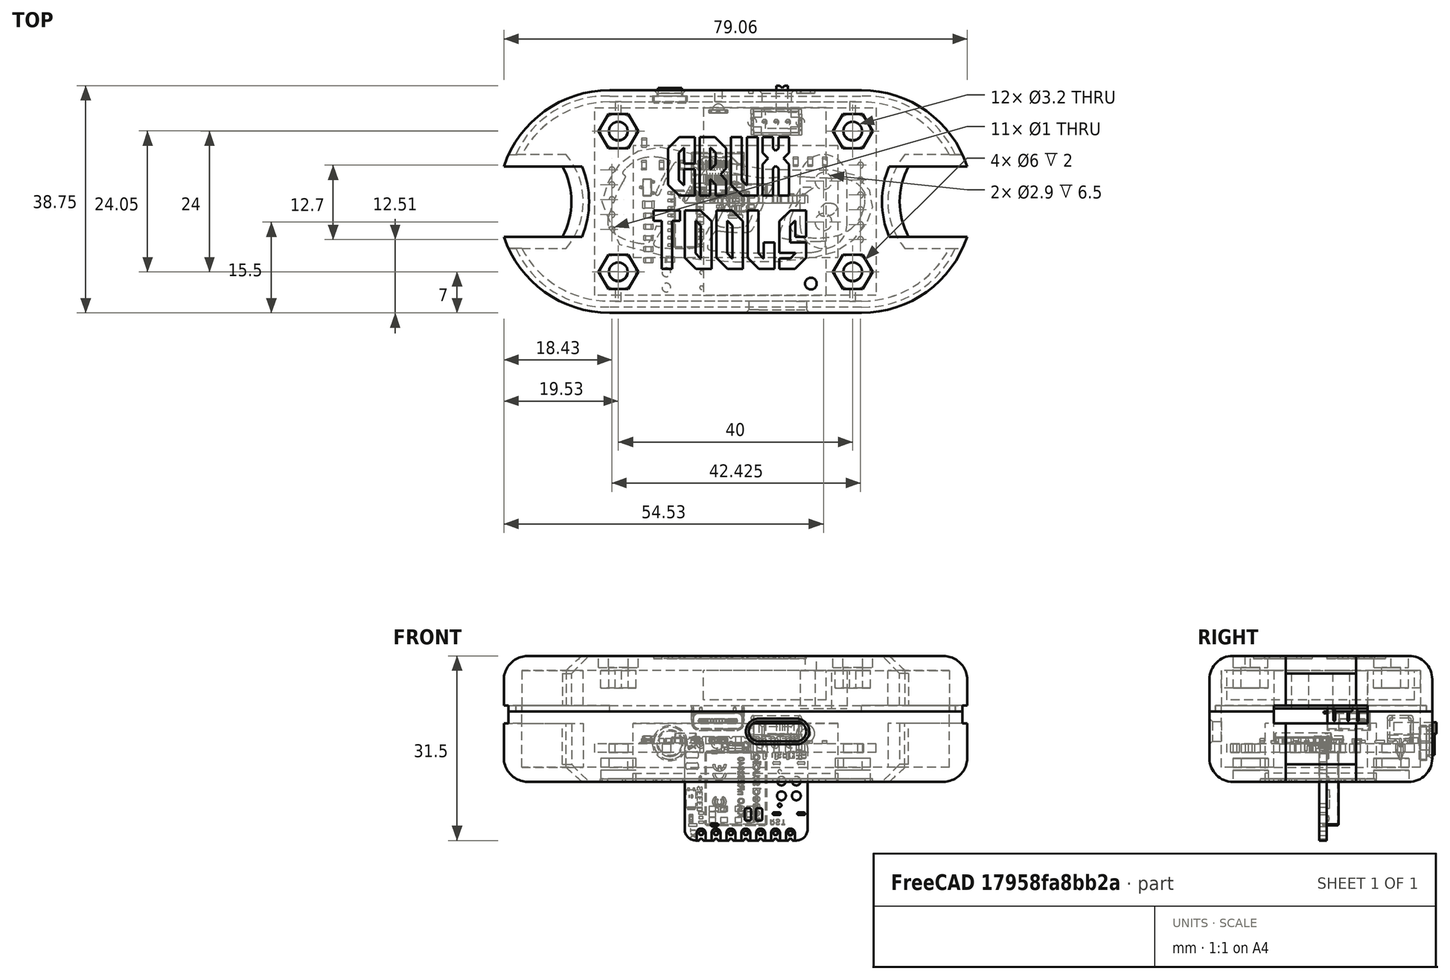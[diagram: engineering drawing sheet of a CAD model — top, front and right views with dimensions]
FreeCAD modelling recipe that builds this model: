
FCSTD DOCUMENT  (FreeCAD 1.0R39285 (Git))
Label: enclosure2
License: All rights reserved
LicenseURL: https://en.wikipedia.org/wiki/All_rights_reserved
objects: Part::Feature×116, Sketcher::SketchObject×53, PartDesign::Pad×51, PartDesign::Body×51, Part::Cut×33, App::Part×17, Part::MultiFuse×8, Part::Extrusion×6, Part::Part2DObjectPython×4, Part::Chamfer×3, Part::FeaturePython×2, Part::Fillet×2, Mesh::Feature×1
note: 484 computed .brp shape members not serialized (recipe doc carries the construction recipe); baked Part::Feature solids carry a one-line shape summary decoded from their .brp

FEATURE [Mesh::Feature] load_cell
  Placement = pos=(0,0,-6.9) rot=(0,0,1;3.14159rad)
FEATURE [Part::Feature] Part__Feature  label="R_0603"
  Placement = pos=(-15.6,10.075,1.595) rot=(0,0,-1;1.5708rad)
  shape: bbox 0.8 x 1.6 x 0.45 mm, 26 faces (baked)
FEATURE [Part::Feature] Part__Feature001  label="R_0604"
  Placement = pos=(-14.8489,-4.2736,1.595) rot=(0,0,1;0rad)
  shape: bbox 1.6 x 0.8 x 0.45 mm, 26 faces (baked)
FEATURE [Part::Feature] Part__Feature002  label="R_0605"
  Placement = pos=(15.22,6.81,1.595) rot=(0,0,-1;1.5708rad)
  shape: bbox 0.8 x 1.6 x 0.45 mm, 26 faces (baked)
FEATURE [Part::Feature] Part__Feature003  label="C_0603"
  Placement = pos=(-3.975,0.675,1.595) rot=(0,0,-1;1.5708rad)
  shape: bbox 0.8 x 1.6 x 0.8 mm, 28 faces (baked)
FEATURE [Part::Feature] Part__Feature004  label="LED-ARRAY-SMD_4P-L3.2-W1.5-H1.0"
  Placement = pos=(-2.94,15.1358,2.095) rot=(0,0,1;0rad)
  shape: bbox 2 x 1 x 1 mm, 5 faces (baked)
FEATURE [Part::Feature] Part__Feature005  label="LED-ARRAY-SMD_4P-L3.2-W1.5-H1.001"
  Placement = pos=(-2.94,15.1358,2.095) rot=(0,0,1;0rad)
  shape: bbox 3.22 x 0.52 x 1.02 mm, 354 faces (baked)
FEATURE [App::Part] LED_ARRAY_SMD_4P_L3_2_W1_5_H1_0  label="LED-ARRAY-SMD_4P-L3.2-W1.5-H1.002"
  Group = -> [Part__Feature004,Part__Feature005]
  Origin = -> Origin020
FEATURE [Part::Feature] Part__Feature006  label="C_0604"
  Placement = pos=(-6.025,6.18,1.595) rot=(0,0,1;1.5708rad)
  shape: bbox 0.8 x 1.6 x 0.8 mm, 28 faces (baked)
FEATURE [Part::Feature] Part__Feature007  label="C_0605"
  Placement = pos=(-11.2489,-9.9886,1.595) rot=(0,0,1;3.14159rad)
  shape: bbox 1.6 x 0.8 x 0.8 mm, 28 faces (baked)
FEATURE [Part::Feature] Part__Feature008  label="R_0606"
  Placement = pos=(12.72,6.81,1.595) rot=(0,0,-1;1.5708rad)
  shape: bbox 0.8 x 1.6 x 0.45 mm, 26 faces (baked)
FEATURE [Part::Feature] Part__Feature009  label="SOIC-16_3.9x9.9mm_P1.27mm"
  Placement = pos=(-8.4989,-3.0036,1.595) rot=(0,0,1;0rad)
  shape: bbox 6 x 9.9 x 1.75 mm, 276 faces (baked)
FEATURE [Part::Feature] Part__Feature010  label="R_0607"
  Placement = pos=(10.22,6.81,1.595) rot=(0,0,-1;1.5708rad)
  shape: bbox 0.8 x 1.6 x 0.45 mm, 26 faces (baked)
FEATURE [Part::Feature] Part__Feature011  label="L_0805"
  Placement = pos=(-14.85,-0.5,1.595) rot=(0,0,1;0rad)
  shape: bbox 2 x 1.25 x 1.25 mm, 28 faces (baked)
FEATURE [Part::Feature] Part__Feature012  label="C_0606"
  Placement = pos=(-14.8489,-6.1786,1.595) rot=(0,0,1;0rad)
  shape: bbox 1.6 x 0.8 x 0.8 mm, 28 faces (baked)
FEATURE [Part::Feature] Part__Feature013  label="Pocket008"
  shape: bbox 2.35 x 3.4 x 1.6 mm, 27 faces (baked)
FEATURE [Part::Feature] Part__Feature014  label="Body001"
  shape: bbox 2.35 x 3.4 x 1.6 mm, 27 faces (baked)
FEATURE [Part::Feature] Part__Feature015  label="Fusion"
  shape: bbox 4.7 x 3.5 x 1.15 mm, 156 faces (baked)
FEATURE [Part::Feature] Part__Feature016  label="Pad007"
  shape: bbox 1.35 x 0.6 x 0.1 mm, 7 faces (baked)
FEATURE [Part::Feature] Part__Feature017  label="Pocket008_(Mirror_#2)"
  shape: bbox 2.35 x 3.4 x 1.6 mm, 27 faces (baked)
FEATURE [Part::Feature] Part__Feature018  label="Body002"
  shape: bbox 2.4 x 4.1 x 1.4 mm, 32 faces (baked)
FEATURE [Part::Feature] Part__Feature019  label="Pocket011"
  shape: bbox 2.4 x 4.1 x 1.4 mm, 17 faces (baked)
FEATURE [Part::Feature] Part__Feature020  label="Pad007_(Mirror_#3)"
  shape: bbox 1.35 x 0.6 x 0.1 mm, 7 faces (baked)
FEATURE [Part::Feature] Part__Feature021  label="Pad007_(Mirror_#5)"
  shape: bbox 1.35 x 0.6 x 0.1 mm, 7 faces (baked)
FEATURE [Part::Feature] Part__Feature022  label="Pad007_(Mirror_#4)"
  shape: bbox 1.35 x 0.6 x 0.1 mm, 7 faces (baked)
FEATURE [App::Part] Panasonic_EVQPUJ_EVQPUA
  Group = -> [Part__Feature013,Part__Feature014,Part__Feature015,Part__Feature016,Part__Feature017,Part__Feature018,Part__Feature019,Part__Feature020,Part__Feature021,Part__Feature022]
  Origin = -> Origin021
  Placement = pos=(-11.125,14.025,1.595) rot=(0,0,1;3.14159rad)
FEATURE [Part::Feature] Part__Feature023  label="R_0608"
  Placement = pos=(-14.8489,-8.0836,1.595) rot=(0,0,1;0rad)
  shape: bbox 1.6 x 0.8 x 0.45 mm, 26 faces (baked)
FEATURE [Part::Feature] Part__Feature024  label="R_0609"
  Placement = pos=(-14.8489,-9.9886,1.595) rot=(0,0,1;0rad)
  shape: bbox 1.6 x 0.8 x 0.45 mm, 26 faces (baked)
FEATURE [Part::Feature] Part__Feature025  label="C_0607"
  Placement = pos=(-15.6,6.18,1.595) rot=(0,0,1;1.5708rad)
  shape: bbox 0.8 x 1.6 x 0.8 mm, 28 faces (baked)
FEATURE [Part::Feature] Part__Feature026  label="C_0608"
  Placement = pos=(-9.025,6.18,1.595) rot=(0,0,1;1.5708rad)
  shape: bbox 0.8 x 1.6 x 0.8 mm, 28 faces (baked)
FEATURE [Part::Feature] Part__Feature027  label="BOSS-EXTRUDE14_8_"
  Placement = pos=(-3.0192,1.09628,5.395) rot=(0,0,1;0rad)
  shape: bbox 0.6 x 1 x 0.3 mm, 6 faces (baked)
FEATURE [Part::Feature] Part__Feature028  label="BOSS-EXTRUDE7_4_"
  Placement = pos=(-3.0192,1.09628,5.395) rot=(0,0,1;0rad)
  shape: bbox 0.3 x 3.784 x 0.75 mm, 6 faces (baked)
FEATURE [Part::Feature] Part__Feature029  label="BOSS-EXTRUDE7_3_"
  Placement = pos=(-3.0192,1.09628,5.395) rot=(0,0,1;0rad)
  shape: bbox 0.3 x 3.784 x 0.75 mm, 6 faces (baked)
FEATURE [Part::Feature] Part__Feature030  label="BOSS-EXTRUDE14_4_"
  Placement = pos=(-3.0192,1.09628,5.395) rot=(0,0,1;0rad)
  shape: bbox 0.3 x 1 x 0.3 mm, 6 faces (baked)
FEATURE [Part::Feature] Part__Feature031  label="BOSS-EXTRUDE14_2_"
  Placement = pos=(-3.0192,1.09628,5.395) rot=(0,0,1;0rad)
  shape: bbox 0.6 x 1 x 0.3 mm, 6 faces (baked)
FEATURE [Part::Feature] Part__Feature032  label="BOSS-EXTRUDE14_11_"
  Placement = pos=(-3.0192,1.09628,5.395) rot=(0,0,1;0rad)
  shape: bbox 0.3 x 1 x 0.3 mm, 6 faces (baked)
FEATURE [Part::Feature] Part__Feature033  label="BOSS-EXTRUDE7_7_"
  Placement = pos=(-3.0192,1.09628,5.395) rot=(0,0,1;0rad)
  shape: bbox 0.3 x 3.784 x 0.75 mm, 6 faces (baked)
FEATURE [Part::Feature] Part__Feature034  label="BOSS-EXTRUDE14_9_"
  Placement = pos=(-3.0192,1.09628,5.395) rot=(0,0,1;0rad)
  shape: bbox 0.3 x 1 x 0.3 mm, 6 faces (baked)
FEATURE [Part::Feature] Part__Feature035  label="BOSS-EXTRUDE14_3_"
  Placement = pos=(-3.0192,1.09628,5.395) rot=(0,0,1;0rad)
  shape: bbox 0.3 x 1 x 0.3 mm, 6 faces (baked)
FEATURE [Part::Feature] Part__Feature036  label="BOSS-EXTRUDE14_7_"
  Placement = pos=(-3.0192,1.09628,5.395) rot=(0,0,1;0rad)
  shape: bbox 0.6 x 1 x 0.3 mm, 6 faces (baked)
FEATURE [Part::Feature] Part__Feature037  label="MIRROR2"
  Placement = pos=(-3.0192,1.09628,5.395) rot=(0,0,1;0rad)
  shape: bbox 6.7 x 4.6 x 0.7 mm, 26 faces (baked)
FEATURE [Part::Feature] Part__Feature038  label="BOSS-EXTRUDE14_5_"
  Placement = pos=(-3.0192,1.09628,5.395) rot=(0,0,1;0rad)
  shape: bbox 0.3 x 1 x 0.3 mm, 6 faces (baked)
FEATURE [Part::Feature] Part__Feature039  label="BOSS-EXTRUDE14_12_"
  Placement = pos=(-3.0192,1.09628,5.395) rot=(0,0,1;0rad)
  shape: bbox 0.3 x 1 x 0.3 mm, 6 faces (baked)
FEATURE [Part::Feature] Part__Feature040  label="BOSS-EXTRUDE7_8_"
  Placement = pos=(-3.0192,1.09628,5.395) rot=(0,0,1;0rad)
  shape: bbox 0.3 x 3.784 x 0.75 mm, 6 faces (baked)
FEATURE [Part::Feature] Part__Feature041  label="BOSS-EXTRUDE7_1_"
  Placement = pos=(-3.0192,1.09628,5.395) rot=(0,0,1;0rad)
  shape: bbox 0.3 x 3.784 x 0.75 mm, 6 faces (baked)
FEATURE [Part::Feature] Part__Feature042  label="BOSS-EXTRUDE14_10_"
  Placement = pos=(-3.0192,1.09628,5.395) rot=(0,0,1;0rad)
  shape: bbox 0.3 x 1 x 0.3 mm, 6 faces (baked)
FEATURE [Part::Feature] Part__Feature043  label="BOSS-EXTRUDE7_9_"
  Placement = pos=(-3.0192,1.09628,5.395) rot=(0,0,1;0rad)
  shape: bbox 0.3 x 3.784 x 0.75 mm, 6 faces (baked)
FEATURE [Part::Feature] Part__Feature044  label="BOSS-EXTRUDE14_6_"
  Placement = pos=(-3.0192,1.09628,5.395) rot=(0,0,1;0rad)
  shape: bbox 0.6 x 1 x 0.3 mm, 6 faces (baked)
FEATURE [Part::Feature] Part__Feature045  label="CHAMFER9"
  Placement = pos=(-3.0192,1.09628,5.395) rot=(0,0,1;0rad)
  shape: bbox 8.94 x 7.3 x 4.2 mm, 103 faces (baked)
FEATURE [Part::Feature] Part__Feature046  label="BOSS-EXTRUDE14_1_"
  Placement = pos=(-3.0192,1.09628,5.395) rot=(0,0,1;0rad)
  shape: bbox 0.3 x 1 x 0.3 mm, 6 faces (baked)
FEATURE [Part::Feature] Part__Feature047  label="BOSS-EXTRUDE7_6_"
  Placement = pos=(-3.0192,1.09628,5.395) rot=(0,0,1;0rad)
  shape: bbox 0.3 x 3.784 x 0.75 mm, 6 faces (baked)
FEATURE [Part::Feature] Part__Feature048  label="BOSS-EXTRUDE7_2_"
  Placement = pos=(-3.0192,1.09628,5.395) rot=(0,0,1;0rad)
  shape: bbox 0.3 x 3.784 x 0.75 mm, 6 faces (baked)
FEATURE [Part::Feature] Part__Feature049  label="CUT-EXTRUDE5"
  Placement = pos=(-3.0192,1.09628,5.395) rot=(0,0,1;0rad)
  shape: bbox 8.867 x 2 x 3.668 mm, 129 faces (baked)
FEATURE [Part::Feature] Part__Feature050  label="BOSS-EXTRUDE7_5_"
  Placement = pos=(-3.0192,1.09628,5.395) rot=(0,0,1;0rad)
  shape: bbox 0.3 x 3.784 x 0.75 mm, 6 faces (baked)
FEATURE [App::Part] USB_TYPE_C_PORT__1_  label="USB TYPE C PORT (1)"
  Group = -> [Part__Feature027,Part__Feature028,Part__Feature029,Part__Feature030,Part__Feature031,Part__Feature032,Part__Feature033,Part__Feature034,Part__Feature035,Part__Feature036,Part__Feature037,Part__Feature038,Part__Feature039,Part__Feature040,Part__Feature041,Part__Feature042,Part__Feature043,Part__Feature044,Part__Feature045,Part__Feature046,Part__Feature047,Part__Feature048,Part__Feature049,+1 more]
  Origin = -> Origin022
  Placement = pos=(-3.0192,1.09628,5.395) rot=(0,0,1;0rad)
FEATURE [App::Part] USB_TYPE_C_PORT  label="USB TYPE C PORT"
  Group = -> [USB_TYPE_C_PORT__1_]
  Origin = -> Origin023
  Placement = pos=(4.31609,13.395,-12.1571) rot=(0.57735,0.57735,-0.57735;2.0944rad)
FEATURE [Part::Feature] Part__Feature051  label="Shield"
  Placement = pos=(-0.225,0,0) rot=(0,0,1;0rad)
  shape: bbox 10.6 x 2.7 x 12.6 mm, 38 faces (baked)
FEATURE [Part::Feature] Part__Feature052  label="Body"
  Placement = pos=(0,0,0.1) rot=(0,0,1;0rad)
  shape: bbox 2.6 x 1.6 x 0.63 mm, 10 faces (baked)
FEATURE [Part::Feature] Part__Feature053  label="Pins"
  shape: bbox 0.44 x 0.44 x 0.1 mm, 6 faces (baked)
FEATURE [Part::Feature] Part__Feature054  label="Pins001"
  shape: bbox 0.44 x 0.44 x 0.1 mm, 6 faces (baked)
FEATURE [Part::Feature] Part__Feature055  label="Pins002"
  shape: bbox 0.44 x 0.44 x 0.1 mm, 6 faces (baked)
FEATURE [Part::Feature] Part__Feature056  label="Pins003"
  shape: bbox 0.44 x 0.44 x 0.1 mm, 6 faces (baked)
FEATURE [App::Part] Pins  label="Pins004"
  Group = -> [Part__Feature053,Part__Feature054,Part__Feature055,Part__Feature056]
  Origin = -> Origin024
FEATURE [App::Part] SKTAAAE010_v1  label="SKTAAAE010 v1"
  Group = -> [Part__Feature052,Pins]
  Origin = -> Origin025
  Placement = pos=(10.4051,1,-11.8268) rot=(-1,0,0;1.5708rad)
FEATURE [Part::Feature] Part__Feature057  label="CAP"
  shape: bbox 0.3048 x 0.3 x 0.3096 mm, 6 faces (baked)
FEATURE [Part::Feature] Part__Feature058  label="CAP001"
  shape: bbox 0.3048 x 0.3 x 0.15 mm, 16 faces (baked)
FEATURE [Part::Feature] Part__Feature059  label="CAP002"
  shape: bbox 0.3048 x 0.3 x 0.15 mm, 16 faces (baked)
FEATURE [App::Part] CAP  label="CAP003"
  Group = -> [Part__Feature057,Part__Feature058,Part__Feature059]
  Origin = -> Origin026
FEATURE [Part::Feature] Part__Feature060  label="ANT1"
  shape: bbox 1.6 x 0.5 x 3.2 mm, 21 faces (baked)
FEATURE [Part::Feature] Part__Feature061  label="ANT002"
  shape: bbox 0.2997 x 0.01 x 0.5004 mm, 10 faces (baked)
FEATURE [Part::Feature] Part__Feature062  label="ANT003"
  shape: bbox 0.05 x 0.01 x 0.5004 mm, 6 faces (baked)
FEATURE [App::Part] ANT1  label="ANT004"
  Group = -> [Part__Feature060,Part__Feature061,Part__Feature062]
  Origin = -> Origin027
FEATURE [Part::Feature] Part__Feature063  label="Silkscreen"
  shape: bbox 0.8405 x 0.01 x 0.5826 mm, 14 faces (baked)
FEATURE [Part::Feature] Part__Feature064  label="Silkscreen001"
  shape: bbox 0.8378 x 0.01 x 0.5436 mm, 10 faces (baked)
FEATURE [Part::Feature] Part__Feature065  label="Silkscreen002"
  shape: bbox 0.6266 x 0.01 x 0.9136 mm, 26 faces (baked)
FEATURE [Part::Feature] Part__Feature066  label="Silkscreen003"
  shape: bbox 0.8636 x 0.01 x 0.6016 mm, 14 faces (baked)
FEATURE [Part::Feature] Part__Feature067  label="Silkscreen004"
  shape: bbox 0.6266 x 0.01 x 0.9136 mm, 26 faces (baked)
FEATURE [Part::Feature] Part__Feature068  label="Silkscreen005"
  shape: bbox 0.5766 x 0.01 x 0.8886 mm, 10 faces (baked)
FEATURE [Part::Feature] Part__Feature069  label="Silkscreen006"
  shape: bbox 0.9136 x 0.01 x 0.6193 mm, 18 faces (baked)
FEATURE [Part::Feature] Part__Feature070  label="Silkscreen007"
  shape: bbox 0.8555 x 0.01 x 0.5936 mm, 20 faces (baked)
FEATURE [Part::Feature] Part__Feature071  label="Silkscreen008"
  shape: bbox 0.6266 x 0.01 x 0.9063 mm, 20 faces (baked)
FEATURE [Part::Feature] Part__Feature072  label="Silkscreen009"
  shape: bbox 0.624 x 0.01 x 0.8886 mm, 14 faces (baked)
FEATURE [Part::Feature] Part__Feature073  label="Silkscreen010"
  shape: bbox 0.624 x 0.01 x 0.9063 mm, 20 faces (baked)
FEATURE [Part::Feature] Part__Feature074  label="Silkscreen011"
  shape: bbox 0.8406 x 0.01 x 0.5851 mm, 14 faces (baked)
FEATURE [Part::Feature] Part__Feature075  label="Silkscreen012"
  shape: bbox 0.635 x 0.01 x 1.397 mm, 10 faces (baked)
FEATURE [App::Part] Silkscreen  label="Silkscreen013"
  Group = -> [Part__Feature063,Part__Feature064,Part__Feature065,Part__Feature066,Part__Feature067,Part__Feature068,Part__Feature069,Part__Feature070,Part__Feature071,Part__Feature072,Part__Feature073,Part__Feature074,Part__Feature075]
  Origin = -> Origin028
FEATURE [Part::Feature] Part__Feature076  label="CAP004"
  Placement = pos=(-1.90636,0,5.2077) rot=(0,0,1;0rad)
  shape: bbox 0.3048 x 0.3 x 0.3096 mm, 6 faces (baked)
FEATURE [Part::Feature] Part__Feature077  label="CAP005"
  Placement = pos=(-1.90636,0,5.2077) rot=(0,0,1;0rad)
  shape: bbox 0.3048 x 0.3 x 0.15 mm, 16 faces (baked)
FEATURE [Part::Feature] Part__Feature078  label="CAP006"
  Placement = pos=(-1.90636,0,5.2077) rot=(0,0,1;0rad)
  shape: bbox 0.3048 x 0.3 x 0.15 mm, 16 faces (baked)
FEATURE [App::Part] CAP001  label="CAP007"
  Group = -> [Part__Feature076,Part__Feature077,Part__Feature078]
  Origin = -> Origin029
FEATURE [Part::Feature] Part__Feature079  label="CAP 3"
  shape: bbox 0.435 x 0.4 x 0.397 mm, 10 faces (baked)
FEATURE [Part::Feature] Part__Feature080  label="CAP 004"
  shape: bbox 0.435 x 0.4 x 0.3 mm, 18 faces (baked)
FEATURE [Part::Feature] Part__Feature081  label="CAP 005"
  shape: bbox 0.435 x 0.4 x 0.3 mm, 18 faces (baked)
FEATURE [App::Part] CAP_3  label="CAP 006"
  Group = -> [Part__Feature079,Part__Feature080,Part__Feature081]
  Origin = -> Origin030
FEATURE [Part::Feature] Part__Feature082  label="LED"
  shape: bbox 0.635 x 0.3 x 0.87 mm, 9 faces (baked)
FEATURE [Part::Feature] Part__Feature083  label="LED001"
  shape: bbox 0.381 x 0.3 x 0.1905 mm, 5 faces (baked)
FEATURE [Part::Feature] Part__Feature084  label="LED002"
  shape: bbox 0.635 x 0.3 x 0.2 mm, 18 faces (baked)
FEATURE [Part::Feature] Part__Feature085  label="LED003"
  shape: bbox 0.635 x 0.3 x 0.2 mm, 8 faces (baked)
FEATURE [App::Part] LED  label="LED004"
  Group = -> [Part__Feature082,Part__Feature083,Part__Feature084,Part__Feature085]
  Origin = -> Origin031
FEATURE [Part::Feature] Part__Feature086  label="USR"
  shape: bbox 1.001 x 0.3 x 1.001 mm, 7 faces (baked)
FEATURE [Part::Feature] Part__Feature087  label="COMPOUND"
  shape: bbox 20.96 x 1.25 x 17.78 mm, 684 faces (baked)
FEATURE [Part::Feature] Part__Feature088  label="COMPOUND001"
  shape: bbox 0.3302 x 0.01 x 0.3302 mm, 6 faces (baked)
FEATURE [Part::Feature] Part__Feature089  label="COMPOUND002"
  shape: bbox 0.3302 x 0.01 x 0.3302 mm, 6 faces (baked)
FEATURE [Part::Feature] Part__Feature090  label="COMPOUND003"
  shape: bbox 0.3302 x 0.01 x 0.3302 mm, 6 faces (baked)
FEATURE [Part::Feature] Part__Feature091  label="COMPOUND004"
  shape: bbox 0.3302 x 0.01 x 0.3302 mm, 6 faces (baked)
FEATURE [Part::Feature] Part__Feature092  label="COMPOUND005"
  shape: bbox 0.2489 x 0.01 x 0.07366 mm, 6 faces (baked)
FEATURE [Part::Feature] Part__Feature093  label="COMPOUND006"
  shape: bbox 0.3658 x 0.01 x 0.3607 mm, 6 faces (baked)
FEATURE [Part::Feature] Part__Feature094  label="COMPOUND007"
  shape: bbox 0.4318 x 0.01 x 0.3658 mm, 6 faces (baked)
FEATURE [Part::Feature] Part__Feature095  label="COMPOUND008"
  shape: bbox 0.4318 x 0.01 x 0.3658 mm, 6 faces (baked)
FEATURE [Part::Feature] Part__Feature096  label="COMPOUND009"
  shape: bbox 1.29 x 0.01 x 0.3861 mm, 6 faces (baked)
FEATURE [Part::Feature] Part__Feature097  label="COMPOUND010"
  shape: bbox 0.3658 x 0.01 x 0.3607 mm, 6 faces (baked)
FEATURE [Part::Feature] Part__Feature098  label="COMPOUND011"
  shape: bbox 0.2489 x 0.01 x 0.1397 mm, 6 faces (baked)
FEATURE [Part::Feature] Part__Feature099  label="COMPOUND012"
  shape: bbox 2.111 x 0.01 x 1.09 mm, 10 faces (baked)
FEATURE [Part::Feature] Part__Feature100  label="COMPOUND013"
  shape: bbox 2.111 x 0.01 x 1.095 mm, 10 faces (baked)
FEATURE [Part::Feature] Part__Feature101  label="COMPOUND014"
  shape: bbox 1.095 x 0.01 x 2.111 mm, 10 faces (baked)
FEATURE [Part::Feature] Part__Feature102  label="COMPOUND015"
  shape: bbox 1.095 x 0.01 x 2.111 mm, 10 faces (baked)
FEATURE [App::Part] COMPOUND  label="COMPOUND016"
  Group = -> [Part__Feature087,Part__Feature088,Part__Feature089,Part__Feature090,Part__Feature091,Part__Feature092,Part__Feature093,Part__Feature094,Part__Feature095,Part__Feature096,Part__Feature097,Part__Feature098,Part__Feature099,Part__Feature100,Part__Feature101,Part__Feature102]
  Origin = -> Origin032
FEATURE [App::Part] PCB__1_  label="PCB (1)"
  Group = -> [CAP,ANT1,Silkscreen,CAP001,CAP_3,LED,Part__Feature086,COMPOUND]
  Origin = -> Origin033
FEATURE [Part::Feature] Part__Feature103  label="SOLID"
  shape: bbox 10.2 x 0.02 x 12.2 mm, 800 faces (baked)
FEATURE [App::Part] XIAO_nRF52840_v3  label="XIAO-nRF52840 v3"
  Group = -> [USB_TYPE_C_PORT,Part__Feature051,SKTAAAE010_v1,PCB__1_,Part__Feature103]
  Origin = -> Origin034
  Placement = pos=(1.04,-3.4715,1.595) rot=(0.57735,-0.57735,-0.57735;2.0944rad)
FEATURE [Part::Feature] Part__Feature104  label="C_0609"
  Placement = pos=(-12.6,6.18,1.595) rot=(0,0,1;1.5708rad)
  shape: bbox 0.8 x 1.6 x 0.8 mm, 28 faces (baked)
FEATURE [Part::Feature] Part__Feature105  label="SOT-23-3"
  Placement = pos=(-15.1,2.4,1.595) rot=(0,0,1;3.14159rad)
  shape: bbox 2.5 x 3 x 1.2 mm, 69 faces (baked)
FEATURE [Part::Feature] Part__Feature106  label="SW_Slide_SPDT_Angled_CK_OS102011MA1Q"
  Placement = pos=(8.95,13.55,1.595) rot=(0,0,1;3.14159rad)
  shape: bbox 8.6 x 4.4 x 7.5 mm, 156 faces (baked)
FEATURE [Part::Feature] Part__Feature107  label="SW_Slide_SPDT_Angled_CK_OS102011MA1Q001"
  Placement = pos=(8.95,13.55,1.595) rot=(0,0,1;3.14159rad)
  shape: bbox 7.7 x 4.4 x 0.6 mm, 14 faces (baked)
FEATURE [Part::Feature] Part__Feature108  label="SW_Slide_SPDT_Angled_CK_OS102011MA1Q002"
  Placement = pos=(8.95,13.55,1.595) rot=(0,0,1;3.14159rad)
  shape: bbox 5.6 x 7.3 x 2 mm, 21 faces (baked)
FEATURE [Part::Feature] Part__Feature109  label="SW_Slide_SPDT_Angled_CK_OS102011MA1Q003"
  Placement = pos=(8.95,13.55,1.595) rot=(0,0,1;3.14159rad)
  shape: bbox 0.5 x 0.3 x 3.6 mm, 8 faces (baked)
FEATURE [Part::Feature] Part__Feature110  label="SW_Slide_SPDT_Angled_CK_OS102011MA1Q004"
  Placement = pos=(8.95,13.55,1.595) rot=(0,0,1;3.14159rad)
  shape: bbox 0.5 x 0.3 x 3.6 mm, 8 faces (baked)
FEATURE [Part::Feature] Part__Feature111  label="SW_Slide_SPDT_Angled_CK_OS102011MA1Q005"
  Placement = pos=(8.95,13.55,1.595) rot=(0,0,1;3.14159rad)
  shape: bbox 0.5 x 0.3 x 3.6 mm, 8 faces (baked)
FEATURE [App::Part] SW_Slide_SPDT_Angled_CK_OS102011MA1Q  label="SW_Slide_SPDT_Angled_CK_OS102011MA1Q006"
  Group = -> [Part__Feature106,Part__Feature107,Part__Feature108,Part__Feature109,Part__Feature110,Part__Feature111]
  Origin = -> Origin035
FEATURE [Part::Feature] Part__Feature112  label="R_0603_1608Metric"
  Placement = pos=(-14.8489,-2.3686,1.595) rot=(0,0,1;0rad)
  shape: bbox 1.6 x 0.8 x 0.45 mm, 26 faces (baked)
FEATURE [Part::Feature] Part__Feature113  label="mito_PCB"
  shape: bbox 48 x 32 x 1.51 mm, 30 faces (baked)
FEATURE [App::Part] mito_1  label="mito 1"
  Group = -> [Part__Feature,Part__Feature001,Part__Feature002,Part__Feature003,LED_ARRAY_SMD_4P_L3_2_W1_5_H1_0,Part__Feature006,Part__Feature007,Part__Feature008,Part__Feature009,Part__Feature010,Part__Feature011,Part__Feature012,Panasonic_EVQPUJ_EVQPUA,Part__Feature023,Part__Feature024,Part__Feature025,Part__Feature026,XIAO_nRF52840_v3,Part__Feature104,Part__Feature105,SW_Slide_SPDT_Angled_CK_OS102011MA1Q,+2 more]
  Origin = -> Origin036
  Placement = pos=(0,-8e-16,-1) rot=(1,0,0;0rad)
FEATURE [Sketcher::SketchObject] Sketch003
  ArcFitTolerance = 1e-06
  AttachmentSupport = -> [XY_Plane037]
  FullyConstrained = true
  MakeInternals = false
  MapMode = 5
  sketch-geometry (4):
    g0: LineSegment StartX=-16 StartY=10.5 StartZ=0 EndX=-16 EndY=-10.5 EndZ=0
    g1: LineSegment StartX=-16 StartY=-10.5 StartZ=0 EndX=16 EndY=-10.5 EndZ=0
    g2: LineSegment StartX=16 StartY=-10.5 StartZ=0 EndX=16 EndY=10.5 EndZ=0
    g3: LineSegment StartX=16 StartY=10.5 StartZ=0 EndX=-16 EndY=10.5 EndZ=0
  constraints (11):
    c: Coincident(g0,g1)
    c: Coincident(g1,g2)
    c: Coincident(g2,g3)
    c: Coincident(g3,g0)
    c: Vertical(g0)
    c: Vertical(g2)
    c: Horizontal(g1)
    c: Horizontal(g3)
    c: Symmetric(g0,g1,g-1)
    c: DistanceX(g3,g3) = 32
    c: DistanceY(g2,g2) = 21
FEATURE [PartDesign::Pad] Pad003
  Direction = (0,0,1)
  Length = 5
  Length2 = 10
  Profile = -> Sketch003
  ReferenceAxis = -> Sketch003 [N_Axis]
  Refine = true
  Suppressed = false
  Type = 0
FEATURE [PartDesign::Body] Body003  label="Battery"
  AllowCompound = false
  Group = -> [Sketch003,Pad003]
  Origin = -> Origin037
  Placement = pos=(5,-2.3e-15,9) rot=(0,0,1;4.71239rad)
  Tip = -> Pad003
FEATURE [Sketcher::SketchObject] Sketch
  ArcFitTolerance = 1e-06
  AttachmentOffset = pos=(0,0,-5) rot=(0,0,1;0rad)
  AttachmentSupport = -> [XY_Plane]
  FullyConstrained = true
  MakeInternals = false
  MapMode = 5
  Placement = pos=(0,0,-5) rot=(0,0,1;0rad)
  sketch-geometry (18):
    g0: ArcOfCircle [constr] CenterX=-21.5 CenterY=1.5e-15 CenterZ=0 NormalX=0 NormalY=0 NormalZ=1 AngleXU=0 Radius=19 StartAngle=1.5708 EndAngle=4.71239
    g1: ArcOfCircle [constr] CenterX=21.5 CenterY=2.06e-14 CenterZ=0 NormalX=0 NormalY=0 NormalZ=1 AngleXU=0 Radius=19 StartAngle=4.71239 EndAngle=7.85398
    g2: LineSegment [constr] StartX=-21.5 StartY=19 StartZ=0 EndX=21.5 EndY=19 EndZ=0
    g3: LineSegment [constr] StartX=-21.5 StartY=-19 StartZ=0 EndX=21.5 EndY=-19 EndZ=0
    g4: LineSegment StartX=-21.5 StartY=19 StartZ=0 EndX=21.5 EndY=19 EndZ=0
    g5: LineSegment StartX=21.5 StartY=-19 StartZ=0 EndX=-21.5 EndY=-19 EndZ=0
    g6: Circle [constr] CenterX=-40.5 CenterY=0 CenterZ=0 NormalX=0 NormalY=0 NormalZ=1 AngleXU=0 Radius=12.5
    g7: Circle [constr] CenterX=40.5 CenterY=0 CenterZ=0 NormalX=0 NormalY=0 NormalZ=1 AngleXU=0 Radius=12.5
    g8: LineSegment StartX=39.5278 StartY=6 StartZ=0 EndX=29.5341 EndY=6 EndZ=0
    g9: LineSegment StartX=39.5278 StartY=-6 StartZ=0 EndX=29.5341 EndY=-6 EndZ=0
    g10: ArcOfCircle CenterX=40.4557 CenterY=1.6e-15 CenterZ=0 NormalX=0 NormalY=0 NormalZ=1 AngleXU=0 Radius=12.4612 StartAngle=2.63923 EndAngle=3.64395
    g11: ArcOfCircle CenterX=21.5 CenterY=2.47e-14 CenterZ=0 NormalX=0 NormalY=0 NormalZ=1 AngleXU=0 Radius=19 StartAngle=0.321289 EndAngle=1.5708
    g12: ArcOfCircle CenterX=21.5 CenterY=1.88e-14 CenterZ=0 NormalX=0 NormalY=0 NormalZ=1 AngleXU=0 Radius=19 StartAngle=4.71239 EndAngle=5.9619
    g13: LineSegment StartX=-39.5278 StartY=6 StartZ=0 EndX=-29.5341 EndY=6 EndZ=0
    g14: LineSegment StartX=-39.5278 StartY=-6 StartZ=0 EndX=-29.5341 EndY=-6 EndZ=0
    g15: ArcOfCircle CenterX=-40.4557 CenterY=1.3e-15 CenterZ=0 NormalX=0 NormalY=0 NormalZ=1 AngleXU=0 Radius=12.4612 StartAngle=5.78082 EndAngle=6.78555
    g16: ArcOfCircle CenterX=-21.5 CenterY=4.1e-15 CenterZ=0 NormalX=0 NormalY=0 NormalZ=1 AngleXU=0 Radius=19 StartAngle=1.5708 EndAngle=2.8203
    g17: ArcOfCircle CenterX=-21.5 CenterY=-1.9e-15 CenterZ=0 NormalX=0 NormalY=0 NormalZ=1 AngleXU=0 Radius=19 StartAngle=3.46288 EndAngle=4.71239
  constraints (48):
    c: Tangent(g0,g2) = 1.5708
    c: Tangent(g0,g3) = -1.5708
    c: Tangent(g1,g2) = 1.5708
    c: Tangent(g1,g3) = -1.5708
    c: DistanceX(g2,g2) = 43
    c: Symmetric(g0,g1,g-2)
    c: Symmetric(g0,g0,g-1)
    c: DistanceY(g0,g0) = 38
    c: Coincident(g4,g0)
    c: Coincident(g4,g1)
    c: Coincident(g5,g1)
    c: Coincident(g5,g0)
    c: PointOnObject(g6,g0)
    c: PointOnObject(g6,g-1)
    c: PointOnObject(g7,g-1)
    c: PointOnObject(g7,g1)
    c: Equal(g7,g6)
    c: Diameter(g7) = 25
    c: PointOnObject(g8,g1)
    c: PointOnObject(g8,g7)
    c: Horizontal(g8)
    c: PointOnObject(g9,g1)
    c: PointOnObject(g9,g7)
    c: Horizontal(g9)
    c: DistanceY(g9,g8) = 12
    c: DistanceY(g-1,g8) = 6
    c: Coincident(g10,g8)
    c: Coincident(g10,g9)
    c: Distance(g10) = 12.52
    c: Tangent(g11,g1) = -1.5708
    c: Coincident(g11,g8)
    c: Tangent(g12,g1) = -1.5708
    c: Coincident(g12,g9)
    c: PointOnObject(g13,g0)
    c: PointOnObject(g13,g6)
    c: Horizontal(g13)
    c: PointOnObject(g14,g0)
    c: PointOnObject(g14,g6)
    c: Horizontal(g14)
    c: DistanceY(g14,g13) = 12
    c: DistanceY(g-1,g13) = 6
    c: Coincident(g15,g13)
    c: Coincident(g15,g14)
    c: Distance(g15) = 12.52
    c: Coincident(g16,g13)
    c: Tangent(g16,g0) = -1.5708
    c: Coincident(g17,g14)
    c: Tangent(g17,g0) = -1.5708
FEATURE [PartDesign::Pad] Pad
  Direction = (0,0,1)
  Length = 12
  Length2 = 10
  Profile = -> Sketch
  ReferenceAxis = -> Sketch [N_Axis]
  Refine = true
  Suppressed = false
  Type = 0
FEATURE [PartDesign::Body] Body  label="bottom_outer"
  AllowCompound = false
  Group = -> [Sketch,Pad]
  Origin = -> Origin
  Tip = -> Pad
FEATURE [Sketcher::SketchObject] Sketch004
  ArcFitTolerance = 1e-06
  AttachmentOffset = pos=(0,0,-2.5) rot=(0,0,1;0rad)
  AttachmentSupport = -> [XY_Plane038]
  FullyConstrained = true
  MakeInternals = false
  MapMode = 5
  Placement = pos=(0,0,-2.5) rot=(0,0,1;0rad)
  sketch-geometry (18):
    g0: ArcOfCircle [constr] CenterX=-21.5 CenterY=8e-16 CenterZ=0 NormalX=0 NormalY=0 NormalZ=1 AngleXU=0 Radius=17 StartAngle=1.5708 EndAngle=4.71239
    g1: ArcOfCircle [constr] CenterX=21.5 CenterY=3.56e-14 CenterZ=0 NormalX=0 NormalY=0 NormalZ=1 AngleXU=0 Radius=17 StartAngle=4.71239 EndAngle=7.85398
    g2: LineSegment [constr] StartX=-21.5 StartY=17 StartZ=0 EndX=21.5 EndY=17 EndZ=0
    g3: LineSegment [constr] StartX=-21.5 StartY=-17 StartZ=0 EndX=21.5 EndY=-17 EndZ=0
    g4: LineSegment StartX=-21.5 StartY=17 StartZ=0 EndX=21.5 EndY=17 EndZ=0
    g5: LineSegment StartX=21.5 StartY=-17 StartZ=0 EndX=-21.5 EndY=-17 EndZ=0
    g6: Circle [constr] CenterX=-38.5 CenterY=0 CenterZ=0 NormalX=0 NormalY=0 NormalZ=1 AngleXU=0 Radius=12.5
    g7: Circle [constr] CenterX=38.5 CenterY=0 CenterZ=0 NormalX=0 NormalY=0 NormalZ=1 AngleXU=0 Radius=12.5
    g8: LineSegment StartX=36.5 StartY=8 StartZ=0 EndX=28.8953 EndY=8 EndZ=0
    g9: LineSegment StartX=36.5 StartY=-8 StartZ=0 EndX=28.8953 EndY=-8 EndZ=0
    g10: ArcOfCircle CenterX=38.4647 CenterY=1.1e-15 CenterZ=0 NormalX=0 NormalY=0 NormalZ=1 AngleXU=0 Radius=12.4729 StartAngle=2.44528 EndAngle=3.8379
    g11: ArcOfCircle CenterX=21.5 CenterY=7.2e-15 CenterZ=0 NormalX=0 NormalY=0 NormalZ=1 AngleXU=0 Radius=17 StartAngle=0.489957 EndAngle=1.5708
    g12: ArcOfCircle CenterX=21.5 CenterY=2.43e-14 CenterZ=0 NormalX=0 NormalY=0 NormalZ=1 AngleXU=0 Radius=17 StartAngle=4.71239 EndAngle=5.79323
    g13: LineSegment StartX=-36.5 StartY=8 StartZ=0 EndX=-28.8953 EndY=8 EndZ=0
    g14: LineSegment StartX=-36.5 StartY=-8 StartZ=0 EndX=-28.8953 EndY=-8 EndZ=0
    g15: ArcOfCircle CenterX=-38.4647 CenterY=1.1e-15 CenterZ=0 NormalX=0 NormalY=0 NormalZ=1 AngleXU=0 Radius=12.4729 StartAngle=5.58687 EndAngle=6.9795
    g16: ArcOfCircle CenterX=-21.5 CenterY=-2.3e-14 CenterZ=0 NormalX=0 NormalY=0 NormalZ=1 AngleXU=0 Radius=17 StartAngle=1.5708 EndAngle=2.65164
    g17: ArcOfCircle CenterX=-21.5 CenterY=-1.27e-14 CenterZ=0 NormalX=0 NormalY=0 NormalZ=1 AngleXU=0 Radius=17 StartAngle=3.63155 EndAngle=4.71239
  constraints (48):
    c: Tangent(g0,g2) = 1.5708
    c: Tangent(g0,g3) = -1.5708
    c: Tangent(g1,g2) = 1.5708
    c: Tangent(g1,g3) = -1.5708
    c: DistanceX(g2,g2) = 43
    c: Symmetric(g0,g1,g-2)
    c: Symmetric(g0,g0,g-1)
    c: DistanceY(g0,g0) = 34
    c: Coincident(g4,g0)
    c: Coincident(g4,g1)
    c: Coincident(g5,g1)
    c: Coincident(g5,g0)
    c: PointOnObject(g6,g0)
    c: PointOnObject(g6,g-1)
    c: PointOnObject(g7,g-1)
    c: PointOnObject(g7,g1)
    c: Equal(g7,g6)
    c: Diameter(g7) = 25
    c: PointOnObject(g8,g1)
    c: PointOnObject(g8,g7)
    c: Horizontal(g8)
    c: PointOnObject(g9,g1)
    c: PointOnObject(g9,g7)
    c: Horizontal(g9)
    c: DistanceY(g9,g8) = 16
    c: Coincident(g10,g8)
    c: Coincident(g10,g9)
    c: Tangent(g11,g1) = -1.5708
    c: Coincident(g11,g8)
    c: Tangent(g12,g1) = -1.5708
    c: Coincident(g12,g9)
    c: PointOnObject(g13,g0)
    c: PointOnObject(g13,g6)
    c: Horizontal(g13)
    c: PointOnObject(g14,g0)
    c: PointOnObject(g14,g6)
    c: Horizontal(g14)
    c: DistanceY(g14,g13) = 16
    c: Coincident(g15,g13)
    c: Coincident(g15,g14)
    c: Coincident(g16,g13)
    c: Tangent(g16,g0) = -1.5708
    c: Coincident(g17,g14)
    c: Tangent(g17,g0) = -1.5708
    c: DistanceY(g-1,g13) = 8
    c: Distance(g15) = 17.37
    c: DistanceY(g-1,g8) = 8
    c: Distance(g10) = 17.37
FEATURE [PartDesign::Pad] Pad004
  Direction = (0,0,1)
  Length = 10
  Length2 = 10
  Profile = -> Sketch004
  ReferenceAxis = -> Sketch004 [N_Axis]
  Refine = true
  Suppressed = false
  Type = 0
FEATURE [PartDesign::Body] Body004  label="bottom_inner"
  AllowCompound = false
  Group = -> [Sketch004,Pad004]
  Origin = -> Origin038
  Tip = -> Pad004
FEATURE [Part::Cut] Cut
  Base = -> Body
  Refine = true
  Tool = -> Body004
FEATURE [Sketcher::SketchObject] Sketch005
  ArcFitTolerance = 1e-06
  AttachmentOffset = pos=(0,0,7) rot=(0,0,1;0rad)
  AttachmentSupport = -> [XY_Plane039]
  FullyConstrained = false
  MakeInternals = false
  MapMode = 5
  Placement = pos=(0,0,7) rot=(0,0,1;0rad)
  sketch-geometry (13):
    g0: ArcOfCircle [constr] CenterX=-21.5 CenterY=-8e-16 CenterZ=0 NormalX=0 NormalY=0 NormalZ=1 AngleXU=0 Radius=17 StartAngle=1.5708 EndAngle=4.71239
    g1: ArcOfCircle [constr] CenterX=21.5 CenterY=1.7e-15 CenterZ=0 NormalX=0 NormalY=0 NormalZ=1 AngleXU=0 Radius=17 StartAngle=4.71239 EndAngle=7.85398
    g2: LineSegment [constr] StartX=-21.5 StartY=17 StartZ=0 EndX=21.5 EndY=17 EndZ=0
    g3: LineSegment StartX=-21.5 StartY=17 StartZ=0 EndX=21.5 EndY=17 EndZ=0
    g4: Circle [constr] CenterX=-38.5 CenterY=0 CenterZ=0 NormalX=0 NormalY=0 NormalZ=1 AngleXU=0 Radius=12.5
    g5: Circle [constr] CenterX=38.5 CenterY=0 CenterZ=0 NormalX=0 NormalY=0 NormalZ=1 AngleXU=0 Radius=12.5
    g6: ArcOfCircle CenterX=21.5 CenterY=-2e-16 CenterZ=0 NormalX=0 NormalY=0 NormalZ=1 AngleXU=0 Radius=17 StartAngle=0.488987 EndAngle=1.5708
    g7: ArcOfCircle CenterX=-21.5 CenterY=-1.3e-15 CenterZ=0 NormalX=0 NormalY=0 NormalZ=1 AngleXU=0 Radius=17 StartAngle=1.5708 EndAngle=2.65022
    g8: LineSegment StartX=-21.5 StartY=18 StartZ=0 EndX=21.5 EndY=18 EndZ=0
    g9: LineSegment StartX=-36.4887 StartY=8.02123 StartZ=0 EndX=-37.4887 EndY=8.02123 EndZ=0
    g10: ArcOfCircle CenterX=-22.003 CenterY=1.00744 CenterZ=0 NormalX=0 NormalY=0 NormalZ=1 AngleXU=0 Radius=17 StartAngle=1.54121 EndAngle=2.71631
    g11: LineSegment StartX=36.5078 StartY=7.98544 StartZ=0 EndX=37.5078 EndY=7.98544 EndZ=0
    g12: ArcOfCircle CenterX=22.0059 CenterY=1.00753 CenterZ=0 NormalX=0 NormalY=0 NormalZ=1 AngleXU=0 Radius=17 StartAngle=0.422964 EndAngle=1.60056
  constraints (33):
    c: Tangent(g0,g2) = 1.5708
    c: Tangent(g1,g2) = 1.5708
    c: DistanceX(g2,g2) = 43
    c: Symmetric(g0,g1,g-2)
    c: Symmetric(g0,g0,g-1)
    c: DistanceY(g0,g0) = 34
    c: Coincident(g3,g0)
    c: Coincident(g3,g1)
    c: PointOnObject(g4,g0)
    c: PointOnObject(g4,g-1)
    c: PointOnObject(g5,g-1)
    c: PointOnObject(g5,g1)
    c: Equal(g5,g4)
    c: Diameter(g5) = 25
    c: PointOnObject(g6,g1)
    c: Tangent(g6,g1) = -1.5708
    c: PointOnObject(g7,g0)
    c: Tangent(g7,g0) = -1.5708
    c: Symmetric(g8,g8,g-2)
    c: Equal(g8,g3)
    c: DistanceY(g0,g8) = 1
    c: Coincident(g9,g7)
    c: Horizontal(g9)
    c: DistanceX(g9,g9) = 1
    c: Coincident(g10,g9)
    c: Coincident(g10,g8)
    c: Equal(g10,g7)
    c: Coincident(g11,g6)
    c: Horizontal(g11)
    c: DistanceX(g11,g11) = 1
    c: Coincident(g12,g11)
    c: Coincident(g12,g8)
    c: Equal(g12,g6)
FEATURE [PartDesign::Pad] Pad005
  Direction = (0,0,1)
  Length = 1
  Length2 = 10
  Profile = -> Sketch005
  ReferenceAxis = -> Sketch005 [N_Axis]
  Refine = true
  Suppressed = false
  Type = 0
FEATURE [PartDesign::Body] Body005  label="Bevel1"
  AllowCompound = false
  Group = -> [Sketch005,Pad005]
  Origin = -> Origin039
  Tip = -> Pad005
FEATURE [Sketcher::SketchObject] Sketch006
  ArcFitTolerance = 1e-06
  AttachmentOffset = pos=(0,0,7) rot=(0,0,1;0rad)
  AttachmentSupport = -> [XY_Plane039]
  FullyConstrained = false
  MakeInternals = false
  MapMode = 5
  Placement = pos=(0,0,7) rot=(0,0,1;0rad)
  sketch-geometry (13):
    g0: ArcOfCircle [constr] CenterX=-21.5 CenterY=-8e-16 CenterZ=0 NormalX=0 NormalY=0 NormalZ=1 AngleXU=0 Radius=17 StartAngle=1.5708 EndAngle=4.71239
    g1: ArcOfCircle [constr] CenterX=21.5 CenterY=1.7e-15 CenterZ=0 NormalX=0 NormalY=0 NormalZ=1 AngleXU=0 Radius=17 StartAngle=4.71239 EndAngle=7.85398
    g2: LineSegment [constr] StartX=-21.5 StartY=17 StartZ=0 EndX=21.5 EndY=17 EndZ=0
    g3: LineSegment StartX=-21.5 StartY=17 StartZ=0 EndX=21.5 EndY=17 EndZ=0
    g4: Circle [constr] CenterX=-38.5 CenterY=0 CenterZ=0 NormalX=0 NormalY=0 NormalZ=1 AngleXU=0 Radius=12.5
    g5: Circle [constr] CenterX=38.5 CenterY=0 CenterZ=0 NormalX=0 NormalY=0 NormalZ=1 AngleXU=0 Radius=12.5
    g6: ArcOfCircle CenterX=21.5 CenterY=-2e-16 CenterZ=0 NormalX=0 NormalY=0 NormalZ=1 AngleXU=0 Radius=17 StartAngle=0.488987 EndAngle=1.5708
    g7: ArcOfCircle CenterX=-21.5 CenterY=-1.3e-15 CenterZ=0 NormalX=0 NormalY=0 NormalZ=1 AngleXU=0 Radius=17 StartAngle=1.5708 EndAngle=2.65022
    g8: LineSegment StartX=-21.5 StartY=18 StartZ=0 EndX=21.5 EndY=18 EndZ=0
    g9: LineSegment StartX=-36.4887 StartY=8.02123 StartZ=0 EndX=-37.4887 EndY=8.02123 EndZ=0
    g10: ArcOfCircle CenterX=-22.003 CenterY=1.00744 CenterZ=0 NormalX=0 NormalY=0 NormalZ=1 AngleXU=0 Radius=17 StartAngle=1.54121 EndAngle=2.71631
    g11: LineSegment StartX=36.5078 StartY=7.98544 StartZ=0 EndX=37.5078 EndY=7.98544 EndZ=0
    g12: ArcOfCircle CenterX=22.0059 CenterY=1.00753 CenterZ=0 NormalX=0 NormalY=0 NormalZ=1 AngleXU=0 Radius=17 StartAngle=0.422964 EndAngle=1.60056
  constraints (33):
    c: Tangent(g0,g2) = 1.5708
    c: Tangent(g1,g2) = 1.5708
    c: DistanceX(g2,g2) = 43
    c: Symmetric(g0,g1,g-2)
    c: Symmetric(g0,g0,g-1)
    c: DistanceY(g0,g0) = 34
    c: Coincident(g3,g0)
    c: Coincident(g3,g1)
    c: PointOnObject(g4,g0)
    c: PointOnObject(g4,g-1)
    c: PointOnObject(g5,g-1)
    c: PointOnObject(g5,g1)
    c: Equal(g5,g4)
    c: Diameter(g5) = 25
    c: PointOnObject(g6,g1)
    c: Tangent(g6,g1) = -1.5708
    c: PointOnObject(g7,g0)
    c: Tangent(g7,g0) = -1.5708
    c: Symmetric(g8,g8,g-2)
    c: Equal(g8,g3)
    c: DistanceY(g0,g8) = 1
    c: Coincident(g9,g7)
    c: Horizontal(g9)
    c: DistanceX(g9,g9) = 1
    c: Coincident(g10,g9)
    c: Coincident(g10,g8)
    c: Equal(g10,g7)
    c: Coincident(g11,g6)
    c: Horizontal(g11)
    c: DistanceX(g11,g11) = 1
    c: Coincident(g12,g11)
    c: Coincident(g12,g8)
    c: Equal(g12,g6)
FEATURE [PartDesign::Pad] Pad006
  Direction = (0,0,1)
  Length = 1
  Length2 = 10
  Profile = -> Sketch006
  ReferenceAxis = -> Sketch006 [N_Axis]
  Refine = true
  Suppressed = false
  Type = 0
FEATURE [PartDesign::Body] Body006  label="Bevel2"
  AllowCompound = false
  Group = -> [Sketch006,Pad006]
  Origin = -> Origin040
  Placement = pos=(0,0,0) rot=(0,0,1;3.14159rad)
  Tip = -> Pad006
FEATURE [Part::MultiFuse] Fusion  label="Fusion001"
  Refine = true
  Shapes = -> [Cut,Body005,Body006]
FEATURE [Sketcher::SketchObject] Sketch007
  ArcFitTolerance = 1e-06
  AttachmentOffset = pos=(0,0,-3) rot=(0,0,1;0rad)
  AttachmentSupport = -> [XY_Plane040]
  FullyConstrained = true
  MakeInternals = false
  MapMode = 5
  Placement = pos=(0,0,-3) rot=(0,0,1;0rad)
  sketch-geometry (1):
    g0: Circle CenterX=-20 CenterY=12 CenterZ=0 NormalX=0 NormalY=0 NormalZ=1 AngleXU=0 Radius=3
  constraints (3):
    c: Diameter(g0) = 6
    c: DistanceY(g-1,g0) = 12
    c: DistanceX(g0,g-1) = 20
FEATURE [PartDesign::Pad] Pad007  label="Pad008"
  Direction = (0,0,1)
  Length = 2
  Length2 = 10
  Profile = -> Sketch007
  ReferenceAxis = -> Sketch007 [N_Axis]
  Refine = true
  Suppressed = false
  Type = 0
FEATURE [PartDesign::Body] Body007  label="Lug1"
  AllowCompound = false
  Group = -> [Sketch007,Pad007]
  Origin = -> Origin041
  Tip = -> Pad007
FEATURE [Sketcher::SketchObject] Sketch008
  ArcFitTolerance = 1e-06
  AttachmentOffset = pos=(0,0,-3) rot=(0,0,1;0rad)
  AttachmentSupport = -> [XY_Plane040]
  FullyConstrained = true
  MakeInternals = false
  MapMode = 5
  Placement = pos=(0,0,-3) rot=(0,0,1;0rad)
  sketch-geometry (1):
    g0: Circle CenterX=20 CenterY=12 CenterZ=0 NormalX=0 NormalY=0 NormalZ=1 AngleXU=0 Radius=3
  constraints (3):
    c: Diameter(g0) = 6
    c: DistanceX(g-1,g0) = 20
    c: DistanceY(g-1,g0) = 12
FEATURE [PartDesign::Pad] Pad008  label="Pad009"
  Direction = (0,0,1)
  Length = 2
  Length2 = 10
  Profile = -> Sketch008
  ReferenceAxis = -> Sketch008 [N_Axis]
  Refine = true
  Suppressed = false
  Type = 0
FEATURE [PartDesign::Body] Body008  label="Lug002"
  AllowCompound = false
  Group = -> [Sketch008,Pad008]
  Origin = -> Origin042
  Tip = -> Pad008
FEATURE [Sketcher::SketchObject] Sketch009
  ArcFitTolerance = 1e-06
  AttachmentOffset = pos=(0,0,-3) rot=(0,0,1;0rad)
  AttachmentSupport = -> [XY_Plane040]
  FullyConstrained = true
  MakeInternals = false
  MapMode = 5
  Placement = pos=(0,0,-3) rot=(0,0,1;0rad)
  sketch-geometry (1):
    g0: Circle CenterX=-20 CenterY=-12 CenterZ=0 NormalX=0 NormalY=0 NormalZ=1 AngleXU=0 Radius=3
  constraints (3):
    c: Diameter(g0) = 6
    c: DistanceY(g0,g-1) = 12
    c: DistanceX(g0,g-1) = 20
FEATURE [PartDesign::Pad] Pad009  label="Pad010"
  Direction = (0,0,1)
  Length = 2
  Length2 = 10
  Profile = -> Sketch009
  ReferenceAxis = -> Sketch009 [N_Axis]
  Refine = true
  Suppressed = false
  Type = 0
FEATURE [PartDesign::Body] Body009  label="Lug003"
  AllowCompound = false
  Group = -> [Sketch009,Pad009]
  Origin = -> Origin043
  Tip = -> Pad009
FEATURE [Sketcher::SketchObject] Sketch010
  ArcFitTolerance = 1e-06
  AttachmentOffset = pos=(0,0,-3) rot=(0,0,1;0rad)
  AttachmentSupport = -> [XY_Plane040]
  FullyConstrained = true
  MakeInternals = false
  MapMode = 5
  Placement = pos=(0,0,-3) rot=(0,0,1;0rad)
  sketch-geometry (1):
    g0: Circle CenterX=20 CenterY=-12 CenterZ=0 NormalX=0 NormalY=0 NormalZ=1 AngleXU=0 Radius=3
  constraints (3):
    c: Diameter(g0) = 6
    c: DistanceY(g0,g-1) = 12
    c: DistanceX(g-1,g0) = 20
FEATURE [PartDesign::Pad] Pad010  label="Pad011"
  Direction = (0,0,1)
  Length = 2
  Length2 = 10
  Profile = -> Sketch010
  ReferenceAxis = -> Sketch010 [N_Axis]
  Refine = true
  Suppressed = false
  Type = 0
FEATURE [PartDesign::Body] Body010  label="Lug004"
  AllowCompound = false
  Group = -> [Sketch010,Pad010]
  Origin = -> Origin044
  Tip = -> Pad010
FEATURE [Part::MultiFuse] Fusion001  label="Fusion002"
  Refine = true
  Shapes = -> [Fusion,Body007,Body008,Body009,Body010]
FEATURE [Sketcher::SketchObject] Sketch011
  ArcFitTolerance = 1e-06
  AttachmentOffset = pos=(0,0,-5) rot=(0,0,1;0rad)
  AttachmentSupport = -> [XY_Plane041]
  FullyConstrained = true
  MakeInternals = false
  MapMode = 5
  Placement = pos=(0,0,-5) rot=(0,0,1;0rad)
  sketch-geometry (1):
    g0: Circle CenterX=20 CenterY=12 CenterZ=0 NormalX=0 NormalY=0 NormalZ=1 AngleXU=0 Radius=3
  constraints (3):
    c: Diameter(g0) = 6
    c: DistanceX(g-1,g0) = 20
    c: DistanceY(g-1,g0) = 12
FEATURE [PartDesign::Pad] Pad011  label="Pad012"
  Direction = (0,0,1)
  Length = 2
  Length2 = 10
  Profile = -> Sketch011
  ReferenceAxis = -> Sketch011 [N_Axis]
  Refine = true
  Suppressed = false
  Type = 0
FEATURE [PartDesign::Body] Body011  label="ScrewHole1"
  AllowCompound = false
  Group = -> [Sketch011,Pad011]
  Origin = -> Origin045
  Tip = -> Pad011
FEATURE [Sketcher::SketchObject] Sketch012
  ArcFitTolerance = 1e-06
  AttachmentOffset = pos=(0,0,-5) rot=(0,0,1;0rad)
  AttachmentSupport = -> [XY_Plane041]
  FullyConstrained = true
  MakeInternals = false
  MapMode = 5
  Placement = pos=(0,0,-5) rot=(0,0,1;0rad)
  sketch-geometry (1):
    g0: Circle CenterX=20 CenterY=-12 CenterZ=0 NormalX=0 NormalY=0 NormalZ=1 AngleXU=0 Radius=3
  constraints (3):
    c: Diameter(g0) = 6
    c: DistanceY(g0,g-1) = 12
    c: DistanceX(g-1,g0) = 20
FEATURE [PartDesign::Pad] Pad012  label="Pad013"
  Direction = (0,0,1)
  Length = 2
  Length2 = 10
  Profile = -> Sketch012
  ReferenceAxis = -> Sketch012 [N_Axis]
  Refine = true
  Suppressed = false
  Type = 0
FEATURE [PartDesign::Body] Body012  label="ScrewHole002"
  AllowCompound = false
  Group = -> [Sketch012,Pad012]
  Origin = -> Origin046
  Tip = -> Pad012
FEATURE [Sketcher::SketchObject] Sketch013
  ArcFitTolerance = 1e-06
  AttachmentOffset = pos=(0,0,-5) rot=(0,0,1;0rad)
  AttachmentSupport = -> [XY_Plane041]
  FullyConstrained = true
  MakeInternals = false
  MapMode = 5
  Placement = pos=(0,0,-5) rot=(0,0,1;0rad)
  sketch-geometry (1):
    g0: Circle CenterX=-20 CenterY=12 CenterZ=0 NormalX=0 NormalY=0 NormalZ=1 AngleXU=0 Radius=3
  constraints (3):
    c: Diameter(g0) = 6
    c: DistanceX(g0,g-1) = 20
    c: DistanceY(g-1,g0) = 12
FEATURE [PartDesign::Pad] Pad013  label="Pad014"
  Direction = (0,0,1)
  Length = 2
  Length2 = 10
  Profile = -> Sketch013
  ReferenceAxis = -> Sketch013 [N_Axis]
  Refine = true
  Suppressed = false
  Type = 0
FEATURE [PartDesign::Body] Body013  label="ScrewHole003"
  AllowCompound = false
  Group = -> [Sketch013,Pad013]
  Origin = -> Origin047
  Tip = -> Pad013
FEATURE [Sketcher::SketchObject] Sketch014
  ArcFitTolerance = 1e-06
  AttachmentOffset = pos=(0,0,-5) rot=(0,0,1;0rad)
  AttachmentSupport = -> [XY_Plane041]
  FullyConstrained = true
  MakeInternals = false
  MapMode = 5
  Placement = pos=(0,0,-5) rot=(0,0,1;0rad)
  sketch-geometry (1):
    g0: Circle CenterX=-20 CenterY=-12 CenterZ=0 NormalX=0 NormalY=0 NormalZ=1 AngleXU=0 Radius=3
  constraints (3):
    c: Diameter(g0) = 6
    c: DistanceY(g0,g-1) = 12
    c: DistanceX(g0,g-1) = 20
FEATURE [PartDesign::Pad] Pad014  label="Pad015"
  Direction = (0,0,1)
  Length = 2
  Length2 = 10
  Profile = -> Sketch014
  ReferenceAxis = -> Sketch014 [N_Axis]
  Refine = true
  Suppressed = false
  Type = 0
FEATURE [PartDesign::Body] Body014  label="ScrewHole004"
  AllowCompound = false
  Group = -> [Sketch014,Pad014]
  Origin = -> Origin048
  Tip = -> Pad014
FEATURE [Part::Cut] Cut001
  Base = -> Fusion001
  Refine = true
  Tool = -> Body011
FEATURE [Part::Cut] Cut002
  Base = -> Cut001
  Refine = true
  Tool = -> Body012
FEATURE [Part::Cut] Cut003
  Base = -> Cut002
  Refine = true
  Tool = -> Body013
FEATURE [Part::Cut] Cut004
  Base = -> Cut003
  Refine = true
  Tool = -> Body014
FEATURE [Sketcher::SketchObject] Sketch015
  ArcFitTolerance = 1e-06
  AttachmentOffset = pos=(0,0,-5) rot=(0,0,1;0rad)
  AttachmentSupport = -> [XY_Plane042]
  FullyConstrained = true
  MakeInternals = false
  MapMode = 5
  Placement = pos=(0,0,-5) rot=(0,0,1;0rad)
  sketch-geometry (1):
    g0: Circle CenterX=-20 CenterY=12 CenterZ=0 NormalX=0 NormalY=0 NormalZ=1 AngleXU=0 Radius=1.6
  constraints (3):
    c: Diameter(g0) = 3.2
    c: DistanceX(g0,g-1) = 20
    c: DistanceY(g-1,g0) = 12
FEATURE [PartDesign::Pad] Pad015  label="Pad016"
  Direction = (0,0,1)
  Length = 5
  Length2 = 10
  Profile = -> Sketch015
  ReferenceAxis = -> Sketch015 [N_Axis]
  Refine = true
  Suppressed = false
  Type = 0
FEATURE [PartDesign::Body] Body015  label="ScrewHoleInner1"
  AllowCompound = false
  Group = -> [Sketch015,Pad015]
  Origin = -> Origin049
  Tip = -> Pad015
FEATURE [Sketcher::SketchObject] Sketch016
  ArcFitTolerance = 1e-06
  AttachmentOffset = pos=(0,0,-5) rot=(0,0,1;0rad)
  AttachmentSupport = -> [XY_Plane042]
  FullyConstrained = true
  MakeInternals = false
  MapMode = 5
  Placement = pos=(0,0,-5) rot=(0,0,1;0rad)
  sketch-geometry (1):
    g0: Circle CenterX=20 CenterY=12 CenterZ=0 NormalX=0 NormalY=0 NormalZ=1 AngleXU=0 Radius=1.6
  constraints (3):
    c: Diameter(g0) = 3.2
    c: DistanceX(g-1,g0) = 20
    c: DistanceY(g-1,g0) = 12
FEATURE [PartDesign::Pad] Pad016  label="Pad017"
  Direction = (0,0,1)
  Length = 5
  Length2 = 10
  Profile = -> Sketch016
  ReferenceAxis = -> Sketch016 [N_Axis]
  Refine = true
  Suppressed = false
  Type = 0
FEATURE [PartDesign::Body] Body016  label="ScrewHoleInner002"
  AllowCompound = false
  Group = -> [Sketch016,Pad016]
  Origin = -> Origin050
  Tip = -> Pad016
FEATURE [Sketcher::SketchObject] Sketch017
  ArcFitTolerance = 1e-06
  AttachmentOffset = pos=(0,0,-5) rot=(0,0,1;0rad)
  AttachmentSupport = -> [XY_Plane042]
  FullyConstrained = true
  MakeInternals = false
  MapMode = 5
  Placement = pos=(0,0,-5) rot=(0,0,1;0rad)
  sketch-geometry (1):
    g0: Circle CenterX=-20 CenterY=-12 CenterZ=0 NormalX=0 NormalY=0 NormalZ=1 AngleXU=0 Radius=1.6
  constraints (3):
    c: Diameter(g0) = 3.2
    c: DistanceX(g0,g-1) = 20
    c: DistanceY(g0,g-1) = 12
FEATURE [PartDesign::Pad] Pad017  label="Pad018"
  Direction = (0,0,1)
  Length = 5
  Length2 = 10
  Profile = -> Sketch017
  ReferenceAxis = -> Sketch017 [N_Axis]
  Refine = true
  Suppressed = false
  Type = 0
FEATURE [PartDesign::Body] Body017  label="ScrewHoleInner003"
  AllowCompound = false
  Group = -> [Sketch017,Pad017]
  Origin = -> Origin051
  Tip = -> Pad017
FEATURE [Sketcher::SketchObject] Sketch018
  ArcFitTolerance = 1e-06
  AttachmentOffset = pos=(0,0,-5) rot=(0,0,1;0rad)
  AttachmentSupport = -> [XY_Plane042]
  FullyConstrained = true
  MakeInternals = false
  MapMode = 5
  Placement = pos=(0,0,-5) rot=(0,0,1;0rad)
  sketch-geometry (1):
    g0: Circle CenterX=20 CenterY=-12 CenterZ=0 NormalX=0 NormalY=0 NormalZ=1 AngleXU=0 Radius=1.6
  constraints (3):
    c: Diameter(g0) = 3.2
    c: DistanceX(g-1,g0) = 20
    c: DistanceY(g0,g-1) = 12
FEATURE [PartDesign::Pad] Pad018  label="Pad019"
  Direction = (0,0,1)
  Length = 5
  Length2 = 10
  Profile = -> Sketch018
  ReferenceAxis = -> Sketch018 [N_Axis]
  Refine = true
  Suppressed = false
  Type = 0
FEATURE [PartDesign::Body] Body018  label="ScrewHoleInner004"
  AllowCompound = false
  Group = -> [Sketch018,Pad018]
  Origin = -> Origin052
  Tip = -> Pad018
FEATURE [Part::Cut] Cut005
  Base = -> Cut004
  Refine = true
  Tool = -> Body015
FEATURE [Part::Cut] Cut006
  Base = -> Cut005
  Refine = true
  Tool = -> Body016
FEATURE [Part::Cut] Cut007
  Base = -> Cut006
  Refine = true
  Tool = -> Body017
FEATURE [Part::Cut] Cut008
  Base = -> Cut007
  Refine = true
  Tool = -> Body018
FEATURE [Sketcher::SketchObject] Sketch019
  ArcFitTolerance = 1e-06
  AttachmentOffset = pos=(0,0,5) rot=(0,0,1;0rad)
  AttachmentSupport = -> [XY_Plane043]
  FullyConstrained = true
  MakeInternals = false
  MapMode = 5
  Placement = pos=(0,0,5) rot=(0,0,1;0rad)
  sketch-geometry (4):
    g0: LineSegment StartX=-40 StartY=8 StartZ=0 EndX=-40 EndY=-8 EndZ=0
    g1: LineSegment StartX=-40 StartY=-8 StartZ=0 EndX=40 EndY=-8 EndZ=0
    g2: LineSegment StartX=40 StartY=-8 StartZ=0 EndX=40 EndY=8 EndZ=0
    g3: LineSegment StartX=40 StartY=8 StartZ=0 EndX=-40 EndY=8 EndZ=0
  constraints (11):
    c: Coincident(g0,g1)
    c: Coincident(g1,g2)
    c: Coincident(g2,g3)
    c: Coincident(g3,g0)
    c: Vertical(g0)
    c: Vertical(g2)
    c: Horizontal(g1)
    c: Horizontal(g3)
    c: Symmetric(g1,g0,g-1)
    c: DistanceY(g0,g0) = 16
    c: DistanceX(g3,g3) = 80
FEATURE [PartDesign::Pad] Pad019  label="Pad020"
  Direction = (0,0,1)
  Length = 4
  Length2 = 10
  Profile = -> Sketch019
  ReferenceAxis = -> Sketch019 [N_Axis]
  Refine = true
  Suppressed = false
  Type = 0
FEATURE [PartDesign::Body] Body019  label="LoadCellCutout"
  AllowCompound = false
  Group = -> [Sketch019,Pad019]
  Origin = -> Origin053
  Tip = -> Pad019
FEATURE [Part::Cut] Cut009  label="Bottom"
  Base = -> Cut008
  Refine = true
  Tool = -> Body019
FEATURE [Sketcher::SketchObject] Sketch020
  ArcFitTolerance = 1e-06
  AttachmentOffset = pos=(0,0,16.5) rot=(0,0,1;0rad)
  AttachmentSupport = -> [XY_Plane044]
  FullyConstrained = true
  MakeInternals = false
  MapMode = 5
  Placement = pos=(0,0,16.5) rot=(0,0,1;0rad)
  sketch-geometry (18):
    g0: ArcOfCircle [constr] CenterX=-21.5 CenterY=1.5e-15 CenterZ=0 NormalX=0 NormalY=0 NormalZ=1 AngleXU=0 Radius=19 StartAngle=1.5708 EndAngle=4.71239
    g1: ArcOfCircle [constr] CenterX=21.5 CenterY=2.06e-14 CenterZ=0 NormalX=0 NormalY=0 NormalZ=1 AngleXU=0 Radius=19 StartAngle=4.71239 EndAngle=7.85398
    g2: LineSegment [constr] StartX=-21.5 StartY=19 StartZ=0 EndX=21.5 EndY=19 EndZ=0
    g3: LineSegment [constr] StartX=-21.5 StartY=-19 StartZ=0 EndX=21.5 EndY=-19 EndZ=0
    g4: LineSegment StartX=-21.5 StartY=19 StartZ=0 EndX=21.5 EndY=19 EndZ=0
    g5: LineSegment StartX=21.5 StartY=-19 StartZ=0 EndX=-21.5 EndY=-19 EndZ=0
    g6: Circle [constr] CenterX=-40.5 CenterY=0 CenterZ=0 NormalX=0 NormalY=0 NormalZ=1 AngleXU=0 Radius=12.5
    g7: Circle [constr] CenterX=40.5 CenterY=0 CenterZ=0 NormalX=0 NormalY=0 NormalZ=1 AngleXU=0 Radius=12.5
    g8: LineSegment StartX=39.5278 StartY=6 StartZ=0 EndX=29.5341 EndY=6 EndZ=0
    g9: LineSegment StartX=39.5278 StartY=-6 StartZ=0 EndX=29.5341 EndY=-6 EndZ=0
    g10: ArcOfCircle CenterX=40.4557 CenterY=1.6e-15 CenterZ=0 NormalX=0 NormalY=0 NormalZ=1 AngleXU=0 Radius=12.4612 StartAngle=2.63923 EndAngle=3.64395
    g11: ArcOfCircle CenterX=21.5 CenterY=2.47e-14 CenterZ=0 NormalX=0 NormalY=0 NormalZ=1 AngleXU=0 Radius=19 StartAngle=0.321289 EndAngle=1.5708
    g12: ArcOfCircle CenterX=21.5 CenterY=1.88e-14 CenterZ=0 NormalX=0 NormalY=0 NormalZ=1 AngleXU=0 Radius=19 StartAngle=4.71239 EndAngle=5.9619
    g13: LineSegment StartX=-39.5278 StartY=6 StartZ=0 EndX=-29.5341 EndY=6 EndZ=0
    g14: LineSegment StartX=-39.5278 StartY=-6 StartZ=0 EndX=-29.5341 EndY=-6 EndZ=0
    g15: ArcOfCircle CenterX=-40.4557 CenterY=1.3e-15 CenterZ=0 NormalX=0 NormalY=0 NormalZ=1 AngleXU=0 Radius=12.4612 StartAngle=5.78082 EndAngle=6.78555
    g16: ArcOfCircle CenterX=-21.5 CenterY=4.1e-15 CenterZ=0 NormalX=0 NormalY=0 NormalZ=1 AngleXU=0 Radius=19 StartAngle=1.5708 EndAngle=2.8203
    g17: ArcOfCircle CenterX=-21.5 CenterY=-1.9e-15 CenterZ=0 NormalX=0 NormalY=0 NormalZ=1 AngleXU=0 Radius=19 StartAngle=3.46288 EndAngle=4.71239
  constraints (48):
    c: Tangent(g0,g2) = 1.5708
    c: Tangent(g0,g3) = -1.5708
    c: Tangent(g1,g2) = 1.5708
    c: Tangent(g1,g3) = -1.5708
    c: DistanceX(g2,g2) = 43
    c: Symmetric(g0,g1,g-2)
    c: Symmetric(g0,g0,g-1)
    c: DistanceY(g0,g0) = 38
    c: Coincident(g4,g0)
    c: Coincident(g4,g1)
    c: Coincident(g5,g1)
    c: Coincident(g5,g0)
    c: PointOnObject(g6,g0)
    c: PointOnObject(g6,g-1)
    c: PointOnObject(g7,g-1)
    c: PointOnObject(g7,g1)
    c: Equal(g7,g6)
    c: Diameter(g7) = 25
    c: PointOnObject(g8,g1)
    c: PointOnObject(g8,g7)
    c: Horizontal(g8)
    c: PointOnObject(g9,g1)
    c: PointOnObject(g9,g7)
    c: Horizontal(g9)
    c: DistanceY(g9,g8) = 12
    c: DistanceY(g-1,g8) = 6
    c: Coincident(g10,g8)
    c: Coincident(g10,g9)
    c: Distance(g10) = 12.52
    c: Tangent(g11,g1) = -1.5708
    c: Coincident(g11,g8)
    c: Tangent(g12,g1) = -1.5708
    c: Coincident(g12,g9)
    c: PointOnObject(g13,g0)
    c: PointOnObject(g13,g6)
    c: Horizontal(g13)
    c: PointOnObject(g14,g0)
    c: PointOnObject(g14,g6)
    c: Horizontal(g14)
    c: DistanceY(g14,g13) = 12
    c: DistanceY(g-1,g13) = 6
    c: Coincident(g15,g13)
    c: Coincident(g15,g14)
    c: Distance(g15) = 12.52
    c: Coincident(g16,g13)
    c: Tangent(g16,g0) = -1.5708
    c: Coincident(g17,g14)
    c: Tangent(g17,g0) = -1.5708
FEATURE [PartDesign::Pad] Pad020  label="Pad021"
  Direction = (0,0,1)
  Length = 9.5
  Length2 = 10
  Profile = -> Sketch020
  ReferenceAxis = -> Sketch020 [N_Axis]
  Refine = true
  Reversed = true
  Suppressed = false
  Type = 0
FEATURE [PartDesign::Body] Body020  label="top_outer"
  AllowCompound = false
  Group = -> [Sketch020,Pad020]
  Origin = -> Origin054
  Tip = -> Pad020
FEATURE [Sketcher::SketchObject] Sketch021
  ArcFitTolerance = 1e-06
  AttachmentOffset = pos=(0,0,14) rot=(0,0,1;0rad)
  AttachmentSupport = -> [XY_Plane045]
  FullyConstrained = true
  MakeInternals = false
  MapMode = 5
  Placement = pos=(0,0,14) rot=(0,0,1;0rad)
  sketch-geometry (18):
    g0: ArcOfCircle [constr] CenterX=-21.5 CenterY=0 CenterZ=0 NormalX=0 NormalY=0 NormalZ=1 AngleXU=0 Radius=17 StartAngle=1.5708 EndAngle=4.71239
    g1: ArcOfCircle [constr] CenterX=21.5 CenterY=-2.1e-15 CenterZ=0 NormalX=0 NormalY=0 NormalZ=1 AngleXU=0 Radius=17 StartAngle=4.71239 EndAngle=7.85398
    g2: LineSegment [constr] StartX=-21.5 StartY=17 StartZ=0 EndX=21.5 EndY=17 EndZ=0
    g3: LineSegment [constr] StartX=-21.5 StartY=-17 StartZ=0 EndX=21.5 EndY=-17 EndZ=0
    g4: LineSegment StartX=-21.5 StartY=17 StartZ=0 EndX=21.5 EndY=17 EndZ=0
    g5: LineSegment StartX=21.5 StartY=-17 StartZ=0 EndX=-21.5 EndY=-17 EndZ=0
    g6: Circle [constr] CenterX=-38.5 CenterY=0 CenterZ=0 NormalX=0 NormalY=0 NormalZ=1 AngleXU=0 Radius=12.5
    g7: Circle [constr] CenterX=38.5 CenterY=0 CenterZ=0 NormalX=0 NormalY=0 NormalZ=1 AngleXU=0 Radius=12.5
    g8: LineSegment StartX=36.5 StartY=8 StartZ=0 EndX=28.8953 EndY=8 EndZ=0
    g9: LineSegment StartX=36.5 StartY=-8 StartZ=0 EndX=28.8953 EndY=-8 EndZ=0
    g10: ArcOfCircle CenterX=38.4647 CenterY=-3e-16 CenterZ=0 NormalX=0 NormalY=0 NormalZ=1 AngleXU=0 Radius=12.4729 StartAngle=2.44528 EndAngle=3.8379
    g11: ArcOfCircle CenterX=21.5 CenterY=-1.58e-14 CenterZ=0 NormalX=0 NormalY=0 NormalZ=1 AngleXU=0 Radius=17 StartAngle=0.489957 EndAngle=1.5708
    g12: ArcOfCircle CenterX=21.5 CenterY=-7.4e-15 CenterZ=0 NormalX=0 NormalY=0 NormalZ=1 AngleXU=0 Radius=17 StartAngle=4.71239 EndAngle=5.79323
    g13: LineSegment StartX=-36.5 StartY=8 StartZ=0 EndX=-28.8953 EndY=8 EndZ=0
    g14: LineSegment StartX=-36.5 StartY=-8 StartZ=0 EndX=-28.8953 EndY=-8 EndZ=0
    g15: ArcOfCircle CenterX=-38.4647 CenterY=-1.5e-15 CenterZ=0 NormalX=0 NormalY=0 NormalZ=1 AngleXU=0 Radius=12.4729 StartAngle=5.58687 EndAngle=6.9795
    g16: ArcOfCircle CenterX=-21.5 CenterY=-4e-15 CenterZ=0 NormalX=0 NormalY=0 NormalZ=1 AngleXU=0 Radius=17 StartAngle=1.5708 EndAngle=2.65164
    g17: ArcOfCircle CenterX=-21.5 CenterY=4e-16 CenterZ=0 NormalX=0 NormalY=0 NormalZ=1 AngleXU=0 Radius=17 StartAngle=3.63155 EndAngle=4.71239
  constraints (48):
    c: Tangent(g0,g2) = 1.5708
    c: Tangent(g0,g3) = -1.5708
    c: Tangent(g1,g2) = 1.5708
    c: Tangent(g1,g3) = -1.5708
    c: DistanceX(g2,g2) = 43
    c: Symmetric(g0,g1,g-2)
    c: Symmetric(g0,g0,g-1)
    c: DistanceY(g0,g0) = 34
    c: Coincident(g4,g0)
    c: Coincident(g4,g1)
    c: Coincident(g5,g1)
    c: Coincident(g5,g0)
    c: PointOnObject(g6,g0)
    c: PointOnObject(g6,g-1)
    c: PointOnObject(g7,g-1)
    c: PointOnObject(g7,g1)
    c: Equal(g7,g6)
    c: Diameter(g7) = 25
    c: PointOnObject(g8,g1)
    c: PointOnObject(g8,g7)
    c: Horizontal(g8)
    c: PointOnObject(g9,g1)
    c: PointOnObject(g9,g7)
    c: Horizontal(g9)
    c: DistanceY(g9,g8) = 16
    c: Coincident(g10,g8)
    c: Coincident(g10,g9)
    c: Tangent(g11,g1) = -1.5708
    c: Coincident(g11,g8)
    c: Tangent(g12,g1) = -1.5708
    c: Coincident(g12,g9)
    c: PointOnObject(g13,g0)
    c: PointOnObject(g13,g6)
    c: Horizontal(g13)
    c: PointOnObject(g14,g0)
    c: PointOnObject(g14,g6)
    c: Horizontal(g14)
    c: DistanceY(g14,g13) = 16
    c: Coincident(g15,g13)
    c: Coincident(g15,g14)
    c: Coincident(g16,g13)
    c: Tangent(g16,g0) = -1.5708
    c: Coincident(g17,g14)
    c: Tangent(g17,g0) = -1.5708
    c: DistanceY(g-1,g13) = 8
    c: Distance(g15) = 17.37
    c: DistanceY(g-1,g8) = 8
    c: Distance(g10) = 17.37
FEATURE [PartDesign::Pad] Pad021  label="Pad022"
  Direction = (0,0,1)
  Length = 7
  Length2 = 10
  Profile = -> Sketch021
  ReferenceAxis = -> Sketch021 [N_Axis]
  Refine = true
  Reversed = true
  Suppressed = false
  Type = 0
FEATURE [PartDesign::Body] Body021  label="top_inner"
  AllowCompound = false
  Group = -> [Sketch021,Pad021]
  Origin = -> Origin055
  Tip = -> Pad021
FEATURE [Part::Cut] Cut010
  Base = -> Body020
  Refine = true
  Tool = -> Body021
FEATURE [Sketcher::SketchObject] Sketch022
  ArcFitTolerance = 1e-06
  AttachmentOffset = pos=(0,0,14) rot=(0,0,1;0rad)
  AttachmentSupport = -> [XY_Plane046]
  FullyConstrained = true
  MakeInternals = false
  MapMode = 5
  Placement = pos=(0,0,14) rot=(0,0,1;0rad)
  sketch-geometry (1):
    g0: Circle CenterX=-20 CenterY=12 CenterZ=0 NormalX=0 NormalY=0 NormalZ=1 AngleXU=0 Radius=3
  constraints (3):
    c: Diameter(g0) = 6
    c: DistanceY(g-1,g0) = 12
    c: DistanceX(g0,g-1) = 20
FEATURE [PartDesign::Pad] Pad022  label="Pad023"
  Direction = (0,0,1)
  Length = 3
  Length2 = 10
  Profile = -> Sketch022
  ReferenceAxis = -> Sketch022 [N_Axis]
  Refine = true
  Reversed = true
  Suppressed = false
  Type = 0
FEATURE [PartDesign::Body] Body022  label="TopLug1"
  AllowCompound = false
  Group = -> [Sketch022,Pad022]
  Origin = -> Origin056
  Tip = -> Pad022
FEATURE [Sketcher::SketchObject] Sketch023
  ArcFitTolerance = 1e-06
  AttachmentOffset = pos=(0,0,14) rot=(0,0,1;0rad)
  AttachmentSupport = -> [XY_Plane046]
  FullyConstrained = true
  MakeInternals = false
  MapMode = 5
  Placement = pos=(0,0,14) rot=(0,0,1;0rad)
  sketch-geometry (1):
    g0: Circle CenterX=20 CenterY=12 CenterZ=0 NormalX=0 NormalY=0 NormalZ=1 AngleXU=0 Radius=3
  constraints (3):
    c: Diameter(g0) = 6
    c: DistanceY(g-1,g0) = 12
    c: DistanceX(g-1,g0) = 20
FEATURE [PartDesign::Pad] Pad023  label="Pad024"
  Direction = (0,0,1)
  Length = 3
  Length2 = 10
  Profile = -> Sketch023
  ReferenceAxis = -> Sketch023 [N_Axis]
  Refine = true
  Reversed = true
  Suppressed = false
  Type = 0
FEATURE [PartDesign::Body] Body023  label="TopLug002"
  AllowCompound = false
  Group = -> [Sketch023,Pad023]
  Origin = -> Origin057
  Tip = -> Pad023
FEATURE [Sketcher::SketchObject] Sketch024
  ArcFitTolerance = 1e-06
  AttachmentOffset = pos=(0,0,14) rot=(0,0,1;0rad)
  AttachmentSupport = -> [XY_Plane046]
  FullyConstrained = true
  MakeInternals = false
  MapMode = 5
  Placement = pos=(0,0,14) rot=(0,0,1;0rad)
  sketch-geometry (1):
    g0: Circle CenterX=-20 CenterY=-12 CenterZ=0 NormalX=0 NormalY=0 NormalZ=1 AngleXU=0 Radius=3
  constraints (3):
    c: Diameter(g0) = 6
    c: DistanceY(g0,g-1) = 12
    c: DistanceX(g0,g-1) = 20
FEATURE [PartDesign::Pad] Pad024  label="Pad025"
  Direction = (0,0,1)
  Length = 3
  Length2 = 10
  Profile = -> Sketch024
  ReferenceAxis = -> Sketch024 [N_Axis]
  Refine = true
  Reversed = true
  Suppressed = false
  Type = 0
FEATURE [PartDesign::Body] Body024  label="TopLug003"
  AllowCompound = false
  Group = -> [Sketch024,Pad024]
  Origin = -> Origin058
  Tip = -> Pad024
FEATURE [Sketcher::SketchObject] Sketch025
  ArcFitTolerance = 1e-06
  AttachmentOffset = pos=(0,0,14) rot=(0,0,1;0rad)
  AttachmentSupport = -> [XY_Plane046]
  FullyConstrained = true
  MakeInternals = false
  MapMode = 5
  Placement = pos=(0,0,14) rot=(0,0,1;0rad)
  sketch-geometry (1):
    g0: Circle CenterX=20 CenterY=-12 CenterZ=0 NormalX=0 NormalY=0 NormalZ=1 AngleXU=0 Radius=3
  constraints (3):
    c: Diameter(g0) = 6
    c: DistanceY(g0,g-1) = 12
    c: DistanceX(g-1,g0) = 20
FEATURE [PartDesign::Pad] Pad025  label="Pad026"
  Direction = (0,0,1)
  Length = 3
  Length2 = 10
  Profile = -> Sketch025
  ReferenceAxis = -> Sketch025 [N_Axis]
  Refine = true
  Reversed = true
  Suppressed = false
  Type = 0
FEATURE [PartDesign::Body] Body025  label="TopLug004"
  AllowCompound = false
  Group = -> [Sketch025,Pad025]
  Origin = -> Origin059
  Tip = -> Pad025
FEATURE [Part::MultiFuse] Fusion002  label="Fusion003"
  Refine = true
  Shapes = -> [Cut010,Body022,Body023,Body024,Body025]
FEATURE [Sketcher::SketchObject] Sketch026
  ArcFitTolerance = 1e-06
  AttachmentOffset = pos=(0,0,14.5) rot=(0,0,1;0rad)
  AttachmentSupport = -> [XY_Plane047]
  FullyConstrained = true
  MakeInternals = false
  MapMode = 5
  Placement = pos=(0,0,14.5) rot=(0,0,1;0rad)
  sketch-geometry (8):
    g0: Circle [constr] CenterX=-20 CenterY=12 CenterZ=0 NormalX=0 NormalY=0 NormalZ=1 AngleXU=0 Radius=3.4
    g1: LineSegment StartX=-18.3 StartY=9.05551 StartZ=0 EndX=-16.6 EndY=12 EndZ=0
    g2: LineSegment StartX=-16.6 StartY=12 StartZ=0 EndX=-18.3 EndY=14.9445 EndZ=0
    g3: LineSegment StartX=-18.3 StartY=14.9445 StartZ=0 EndX=-21.7 EndY=14.9445 EndZ=0
    g4: LineSegment StartX=-21.7 StartY=14.9445 StartZ=0 EndX=-23.4 EndY=12 EndZ=0
    g5: LineSegment StartX=-23.4 StartY=12 StartZ=0 EndX=-21.7 EndY=9.05551 EndZ=0
    g6: LineSegment StartX=-21.7 StartY=9.05551 StartZ=0 EndX=-18.3 EndY=9.05551 EndZ=0
    g7: Circle [constr] CenterX=-20 CenterY=12 CenterZ=0 NormalX=0 NormalY=0 NormalZ=1 AngleXU=0 Radius=3.4
  constraints (19):
    c: Diameter(g0) = 6.8
    c: DistanceY(g-1,g0) = 12
    c: DistanceX(g0,g-1) = 20
    c: Coincident(g1,g2)
    c: Coincident(g2,g3)
    c: Coincident(g3,g4)
    c: Coincident(g4,g5)
    c: Coincident(g5,g6)
    c: Coincident(g6,g1)
    c: Equal(g1, g2-g6) x5
    c: PointOnObject(g1,g7)
    c: PointOnObject(g2,g7)
    c: PointOnObject(g3,g7)
    c: PointOnObject(g4,g7)
    c: PointOnObject(g5,g7)
    c: PointOnObject(g6,g7)
    c: Coincident(g7,g0)
    c: PointOnObject(g6,g0)
    c: Vertical(g1,g2)
FEATURE [Sketcher::SketchObject] Sketch027
  ArcFitTolerance = 1e-06
  AttachmentOffset = pos=(0,0,14.5) rot=(0,0,1;0rad)
  AttachmentSupport = -> [XY_Plane048]
  FullyConstrained = true
  MakeInternals = false
  MapMode = 5
  Placement = pos=(0,0,14.5) rot=(0,0,1;0rad)
  sketch-geometry (8):
    g0: Circle [constr] CenterX=20 CenterY=12 CenterZ=0 NormalX=0 NormalY=0 NormalZ=1 AngleXU=0 Radius=3.4
    g1: LineSegment StartX=21.7 StartY=9.05551 StartZ=0 EndX=23.4 EndY=12 EndZ=0
    g2: LineSegment StartX=23.4 StartY=12 StartZ=0 EndX=21.7 EndY=14.9445 EndZ=0
    g3: LineSegment StartX=21.7 StartY=14.9445 StartZ=0 EndX=18.3 EndY=14.9445 EndZ=0
    g4: LineSegment StartX=18.3 StartY=14.9445 StartZ=0 EndX=16.6 EndY=12 EndZ=0
    g5: LineSegment StartX=16.6 StartY=12 StartZ=0 EndX=18.3 EndY=9.05551 EndZ=0
    g6: LineSegment StartX=18.3 StartY=9.05551 StartZ=0 EndX=21.7 EndY=9.05551 EndZ=0
    g7: Circle [constr] CenterX=20 CenterY=12 CenterZ=0 NormalX=0 NormalY=0 NormalZ=1 AngleXU=0 Radius=3.4
  constraints (19):
    c: Diameter(g0) = 6.8
    c: DistanceY(g-1,g0) = 12
    c: DistanceX(g-1,g0) = 20
    c: Coincident(g1,g2)
    c: Coincident(g2,g3)
    c: Coincident(g3,g4)
    c: Coincident(g4,g5)
    c: Coincident(g5,g6)
    c: Coincident(g6,g1)
    c: Equal(g1, g2-g6) x5
    c: PointOnObject(g1,g7)
    c: PointOnObject(g2,g7)
    c: PointOnObject(g3,g7)
    c: PointOnObject(g4,g7)
    c: PointOnObject(g5,g7)
    c: PointOnObject(g6,g7)
    c: Coincident(g7,g0)
    c: PointOnObject(g6,g0)
    c: Vertical(g1,g2)
FEATURE [Sketcher::SketchObject] Sketch028
  ArcFitTolerance = 1e-06
  AttachmentOffset = pos=(0,0,14.5) rot=(0,0,1;0rad)
  AttachmentSupport = -> [XY_Plane049]
  FullyConstrained = true
  MakeInternals = false
  MapMode = 5
  Placement = pos=(0,0,14.5) rot=(0,0,1;0rad)
  sketch-geometry (8):
    g0: Circle [constr] CenterX=-20 CenterY=-12 CenterZ=0 NormalX=0 NormalY=0 NormalZ=1 AngleXU=0 Radius=3.4
    g1: LineSegment StartX=-18.3 StartY=-14.9445 StartZ=0 EndX=-16.6 EndY=-12 EndZ=0
    g2: LineSegment StartX=-16.6 StartY=-12 StartZ=0 EndX=-18.3 EndY=-9.05551 EndZ=0
    g3: LineSegment StartX=-18.3 StartY=-9.05551 StartZ=0 EndX=-21.7 EndY=-9.05551 EndZ=0
    g4: LineSegment StartX=-21.7 StartY=-9.05551 StartZ=0 EndX=-23.4 EndY=-12 EndZ=0
    g5: LineSegment StartX=-23.4 StartY=-12 StartZ=0 EndX=-21.7 EndY=-14.9445 EndZ=0
    g6: LineSegment StartX=-21.7 StartY=-14.9445 StartZ=0 EndX=-18.3 EndY=-14.9445 EndZ=0
    g7: Circle [constr] CenterX=-20 CenterY=-12 CenterZ=0 NormalX=0 NormalY=0 NormalZ=1 AngleXU=0 Radius=3.4
  constraints (19):
    c: Diameter(g0) = 6.8
    c: DistanceY(g0,g-1) = 12
    c: DistanceX(g0,g-1) = 20
    c: Coincident(g1,g2)
    c: Coincident(g2,g3)
    c: Coincident(g3,g4)
    c: Coincident(g4,g5)
    c: Coincident(g5,g6)
    c: Coincident(g6,g1)
    c: Equal(g1, g2-g6) x5
    c: PointOnObject(g1,g7)
    c: PointOnObject(g2,g7)
    c: PointOnObject(g3,g7)
    c: PointOnObject(g4,g7)
    c: PointOnObject(g5,g7)
    c: PointOnObject(g6,g7)
    c: Coincident(g7,g0)
    c: PointOnObject(g6,g0)
    c: Vertical(g1,g2)
FEATURE [Sketcher::SketchObject] Sketch029
  ArcFitTolerance = 1e-06
  AttachmentOffset = pos=(0,0,14.5) rot=(0,0,1;0rad)
  AttachmentSupport = -> [XY_Plane050]
  FullyConstrained = true
  MakeInternals = false
  MapMode = 5
  Placement = pos=(0,0,14.5) rot=(0,0,1;0rad)
  sketch-geometry (8):
    g0: Circle [constr] CenterX=20 CenterY=-12 CenterZ=0 NormalX=0 NormalY=0 NormalZ=1 AngleXU=0 Radius=3.4
    g1: LineSegment StartX=21.7 StartY=-14.9445 StartZ=0 EndX=23.4 EndY=-12 EndZ=0
    g2: LineSegment StartX=23.4 StartY=-12 StartZ=0 EndX=21.7 EndY=-9.05551 EndZ=0
    g3: LineSegment StartX=21.7 StartY=-9.05551 StartZ=0 EndX=18.3 EndY=-9.05551 EndZ=0
    g4: LineSegment StartX=18.3 StartY=-9.05551 StartZ=0 EndX=16.6 EndY=-12 EndZ=0
    g5: LineSegment StartX=16.6 StartY=-12 StartZ=0 EndX=18.3 EndY=-14.9445 EndZ=0
    g6: LineSegment StartX=18.3 StartY=-14.9445 StartZ=0 EndX=21.7 EndY=-14.9445 EndZ=0
    g7: Circle [constr] CenterX=20 CenterY=-12 CenterZ=0 NormalX=0 NormalY=0 NormalZ=1 AngleXU=0 Radius=3.4
  constraints (19):
    c: Diameter(g0) = 6.8
    c: DistanceY(g0,g-1) = 12
    c: DistanceX(g-1,g0) = 20
    c: Coincident(g1,g2)
    c: Coincident(g2,g3)
    c: Coincident(g3,g4)
    c: Coincident(g4,g5)
    c: Coincident(g5,g6)
    c: Coincident(g6,g1)
    c: Equal(g1, g2-g6) x5
    c: PointOnObject(g1,g7)
    c: PointOnObject(g2,g7)
    c: PointOnObject(g3,g7)
    c: PointOnObject(g4,g7)
    c: PointOnObject(g5,g7)
    c: PointOnObject(g6,g7)
    c: Coincident(g7,g0)
    c: PointOnObject(g6,g0)
    c: Vertical(g5,g3)
FEATURE [PartDesign::Pad] Pad026  label="Pad027"
  Direction = (0,0,1)
  Length = 2
  Length2 = 10
  Profile = -> Sketch026
  ReferenceAxis = -> Sketch026 [N_Axis]
  Refine = true
  Suppressed = false
  Type = 0
FEATURE [PartDesign::Body] Body026  label="ScrewHoleTop1"
  AllowCompound = false
  Group = -> [Sketch026,Pad026]
  Origin = -> Origin060
  Tip = -> Pad026
FEATURE [PartDesign::Pad] Pad027  label="Pad028"
  Direction = (0,0,1)
  Length = 2
  Length2 = 10
  Profile = -> Sketch027
  ReferenceAxis = -> Sketch027 [N_Axis]
  Refine = true
  Suppressed = false
  Type = 0
FEATURE [PartDesign::Body] Body027  label="ScrewHoleTop2"
  AllowCompound = false
  Group = -> [Sketch027,Pad027]
  Origin = -> Origin061
  Tip = -> Pad027
FEATURE [PartDesign::Pad] Pad028  label="Pad029"
  Direction = (0,0,1)
  Length = 2
  Length2 = 10
  Profile = -> Sketch028
  ReferenceAxis = -> Sketch028 [N_Axis]
  Refine = true
  Suppressed = false
  Type = 0
FEATURE [PartDesign::Body] Body028  label="ScrewHoleTop3"
  AllowCompound = false
  Group = -> [Sketch028,Pad028]
  Origin = -> Origin062
  Tip = -> Pad028
FEATURE [PartDesign::Pad] Pad029  label="Pad030"
  Direction = (0,0,1)
  Length = 2
  Length2 = 10
  Profile = -> Sketch029
  ReferenceAxis = -> Sketch029 [N_Axis]
  Refine = true
  Suppressed = false
  Type = 0
FEATURE [PartDesign::Body] Body029  label="ScrewHoleTop4"
  AllowCompound = false
  Group = -> [Sketch029,Pad029]
  Origin = -> Origin063
  Tip = -> Pad029
FEATURE [Part::Cut] Cut011
  Base = -> Fusion002
  Refine = true
  Tool = -> Body026
FEATURE [Part::Cut] Cut012
  Base = -> Cut011
  Refine = true
  Tool = -> Body027
FEATURE [Part::Cut] Cut013
  Base = -> Cut012
  Refine = true
  Tool = -> Body028
FEATURE [Part::Cut] Cut014
  Base = -> Cut013
  Refine = true
  Tool = -> Body029
FEATURE [Sketcher::SketchObject] Sketch030
  ArcFitTolerance = 1e-06
  AttachmentOffset = pos=(0,0,16.5) rot=(0,0,1;0rad)
  AttachmentSupport = -> [XY_Plane051]
  FullyConstrained = true
  MakeInternals = false
  MapMode = 5
  Placement = pos=(0,0,16.5) rot=(0,0,1;0rad)
  sketch-geometry (1):
    g0: Circle CenterX=-20 CenterY=12 CenterZ=0 NormalX=0 NormalY=0 NormalZ=1 AngleXU=0 Radius=1.6
  constraints (3):
    c: Diameter(g0) = 3.2
    c: DistanceY(g-1,g0) = 12
    c: DistanceX(g0,g-1) = 20
FEATURE [PartDesign::Pad] Pad030  label="Pad031"
  Direction = (0,0,1)
  Length = 10
  Length2 = 10
  Profile = -> Sketch030
  ReferenceAxis = -> Sketch030 [N_Axis]
  Refine = true
  Reversed = true
  Suppressed = false
  Type = 0
FEATURE [PartDesign::Body] Body030  label="ScrewHoleInnerTop1"
  AllowCompound = false
  Group = -> [Sketch030,Pad030]
  Origin = -> Origin064
  Tip = -> Pad030
FEATURE [Sketcher::SketchObject] Sketch031
  ArcFitTolerance = 1e-06
  AttachmentOffset = pos=(0,0,16.5) rot=(0,0,1;0rad)
  AttachmentSupport = -> [XY_Plane051]
  FullyConstrained = true
  MakeInternals = false
  MapMode = 5
  Placement = pos=(0,0,16.5) rot=(0,0,1;0rad)
  sketch-geometry (1):
    g0: Circle CenterX=20 CenterY=12 CenterZ=0 NormalX=0 NormalY=0 NormalZ=1 AngleXU=0 Radius=1.6
  constraints (3):
    c: Diameter(g0) = 3.2
    c: DistanceY(g-1,g0) = 12
    c: DistanceX(g-1,g0) = 20
FEATURE [PartDesign::Pad] Pad031  label="Pad032"
  Direction = (0,0,1)
  Length = 10
  Length2 = 10
  Profile = -> Sketch031
  ReferenceAxis = -> Sketch031 [N_Axis]
  Refine = true
  Reversed = true
  Suppressed = false
  Type = 0
FEATURE [PartDesign::Body] Body031  label="ScrewHoleInnerTop002"
  AllowCompound = false
  Group = -> [Sketch031,Pad031]
  Origin = -> Origin065
  Tip = -> Pad031
FEATURE [Sketcher::SketchObject] Sketch032
  ArcFitTolerance = 1e-06
  AttachmentOffset = pos=(0,0,16.5) rot=(0,0,1;0rad)
  AttachmentSupport = -> [XY_Plane051]
  FullyConstrained = true
  MakeInternals = false
  MapMode = 5
  Placement = pos=(0,0,16.5) rot=(0,0,1;0rad)
  sketch-geometry (1):
    g0: Circle CenterX=-20 CenterY=-12 CenterZ=0 NormalX=0 NormalY=0 NormalZ=1 AngleXU=0 Radius=1.6
  constraints (3):
    c: Diameter(g0) = 3.2
    c: DistanceY(g0,g-1) = 12
    c: DistanceX(g0,g-1) = 20
FEATURE [PartDesign::Pad] Pad032  label="Pad033"
  Direction = (0,0,1)
  Length = 10
  Length2 = 10
  Profile = -> Sketch032
  ReferenceAxis = -> Sketch032 [N_Axis]
  Refine = true
  Reversed = true
  Suppressed = false
  Type = 0
FEATURE [PartDesign::Body] Body032  label="ScrewHoleInnerTop003"
  AllowCompound = false
  Group = -> [Sketch032,Pad032]
  Origin = -> Origin066
  Tip = -> Pad032
FEATURE [Sketcher::SketchObject] Sketch033
  ArcFitTolerance = 1e-06
  AttachmentOffset = pos=(0,0,16.5) rot=(0,0,1;0rad)
  AttachmentSupport = -> [XY_Plane051]
  FullyConstrained = true
  MakeInternals = false
  MapMode = 5
  Placement = pos=(0,0,16.5) rot=(0,0,1;0rad)
  sketch-geometry (1):
    g0: Circle CenterX=20 CenterY=-12 CenterZ=0 NormalX=0 NormalY=0 NormalZ=1 AngleXU=0 Radius=1.6
  constraints (3):
    c: Diameter(g0) = 3.2
    c: DistanceY(g0,g-1) = 12
    c: DistanceX(g-1,g0) = 20
FEATURE [PartDesign::Pad] Pad033  label="Pad034"
  Direction = (0,0,1)
  Length = 10
  Length2 = 10
  Profile = -> Sketch033
  ReferenceAxis = -> Sketch033 [N_Axis]
  Refine = true
  Reversed = true
  Suppressed = false
  Type = 0
FEATURE [PartDesign::Body] Body033  label="ScrewHoleInnerTop004"
  AllowCompound = false
  Group = -> [Sketch033,Pad033]
  Origin = -> Origin067
  Tip = -> Pad033
FEATURE [Part::Cut] Cut015
  Base = -> Cut014
  Refine = true
  Tool = -> Body030
FEATURE [Part::Cut] Cut016
  Base = -> Cut015
  Refine = true
  Tool = -> Body031
FEATURE [Part::Cut] Cut017
  Base = -> Cut016
  Refine = true
  Tool = -> Body032
FEATURE [Part::Cut] Cut018
  Base = -> Cut017
  Refine = true
  Tool = -> Body033
FEATURE [Sketcher::SketchObject] Sketch034
  ArcFitTolerance = 1e-06
  AttachmentOffset = pos=(0,0,14) rot=(0,0,1;0rad)
  AttachmentSupport = -> [XY_Plane052]
  FullyConstrained = true
  MakeInternals = false
  MapMode = 5
  Placement = pos=(0,0,14) rot=(0,0,1;0rad)
  sketch-geometry (4):
    g0: LineSegment StartX=-20.5 StartY=17.5 StartZ=0 EndX=-20.5 EndY=14.5 EndZ=0
    g1: LineSegment StartX=-20.5 StartY=14.5 StartZ=0 EndX=-19.5 EndY=14.5 EndZ=0
    g2: LineSegment StartX=-19.5 StartY=14.5 StartZ=0 EndX=-19.5 EndY=17.5 EndZ=0
    g3: LineSegment StartX=-19.5 StartY=17.5 StartZ=0 EndX=-20.5 EndY=17.5 EndZ=0
  constraints (12):
    c: Coincident(g0,g1)
    c: Coincident(g1,g2)
    c: Coincident(g2,g3)
    c: Coincident(g3,g0)
    c: Vertical(g0)
    c: Vertical(g2)
    c: Horizontal(g1)
    c: Horizontal(g3)
    c: DistanceX(g3,g3) = 1
    c: DistanceY(g2,g2) = 3
    c: DistanceX(g1,g-1) = 19.5
    c: DistanceY(g-1,g1) = 14.5
FEATURE [PartDesign::Pad] Pad034  label="Pad035"
  Direction = (0,0,1)
  Length = 3
  Length2 = 10
  Profile = -> Sketch034
  ReferenceAxis = -> Sketch034 [N_Axis]
  Refine = true
  Reversed = true
  Suppressed = false
  Type = 0
FEATURE [PartDesign::Body] Body034  label="StandoffSupport1"
  AllowCompound = false
  Group = -> [Sketch034,Pad034]
  Origin = -> Origin068
  Tip = -> Pad034
FEATURE [Sketcher::SketchObject] Sketch035
  ArcFitTolerance = 1e-06
  AttachmentOffset = pos=(0,0,14) rot=(0,0,1;0rad)
  AttachmentSupport = -> [XY_Plane052]
  FullyConstrained = true
  MakeInternals = false
  MapMode = 5
  Placement = pos=(0,0,14) rot=(0,0,1;0rad)
  sketch-geometry (4):
    g0: LineSegment StartX=19.5 StartY=17.5 StartZ=0 EndX=19.5 EndY=14.5 EndZ=0
    g1: LineSegment StartX=19.5 StartY=14.5 StartZ=0 EndX=20.5 EndY=14.5 EndZ=0
    g2: LineSegment StartX=20.5 StartY=14.5 StartZ=0 EndX=20.5 EndY=17.5 EndZ=0
    g3: LineSegment StartX=20.5 StartY=17.5 StartZ=0 EndX=19.5 EndY=17.5 EndZ=0
  constraints (12):
    c: Coincident(g0,g1)
    c: Coincident(g1,g2)
    c: Coincident(g2,g3)
    c: Coincident(g3,g0)
    c: Vertical(g0)
    c: Vertical(g2)
    c: Horizontal(g1)
    c: Horizontal(g3)
    c: DistanceX(g3,g3) = 1
    c: DistanceY(g2,g2) = 3
    c: DistanceX(g-1,g0) = 19.5
    c: DistanceY(g-1,g0) = 14.5
FEATURE [PartDesign::Pad] Pad035  label="Pad036"
  Direction = (0,0,1)
  Length = 3
  Length2 = 10
  Profile = -> Sketch035
  ReferenceAxis = -> Sketch035 [N_Axis]
  Refine = true
  Reversed = true
  Suppressed = false
  Type = 0
FEATURE [PartDesign::Body] Body035  label="StandoffSupport002"
  AllowCompound = false
  Group = -> [Sketch035,Pad035]
  Origin = -> Origin069
  Tip = -> Pad035
FEATURE [Sketcher::SketchObject] Sketch036
  ArcFitTolerance = 1e-06
  AttachmentOffset = pos=(0,0,14) rot=(0,0,1;0rad)
  AttachmentSupport = -> [XY_Plane052]
  FullyConstrained = true
  MakeInternals = false
  MapMode = 5
  Placement = pos=(0,0,14) rot=(0,0,1;0rad)
  sketch-geometry (4):
    g0: LineSegment StartX=-20.5 StartY=-14.5 StartZ=0 EndX=-20.5 EndY=-17.5 EndZ=0
    g1: LineSegment StartX=-20.5 StartY=-17.5 StartZ=0 EndX=-19.5 EndY=-17.5 EndZ=0
    g2: LineSegment StartX=-19.5 StartY=-17.5 StartZ=0 EndX=-19.5 EndY=-14.5 EndZ=0
    g3: LineSegment StartX=-19.5 StartY=-14.5 StartZ=0 EndX=-20.5 EndY=-14.5 EndZ=0
  constraints (12):
    c: Coincident(g0,g1)
    c: Coincident(g1,g2)
    c: Coincident(g2,g3)
    c: Coincident(g3,g0)
    c: Vertical(g0)
    c: Vertical(g2)
    c: Horizontal(g1)
    c: Horizontal(g3)
    c: DistanceX(g3,g3) = 1
    c: DistanceY(g2,g2) = 3
    c: DistanceX(g2,g-1) = 19.5
    c: DistanceY(g2,g-1) = 14.5
FEATURE [PartDesign::Pad] Pad036  label="Pad037"
  Direction = (0,0,1)
  Length = 3
  Length2 = 10
  Profile = -> Sketch036
  ReferenceAxis = -> Sketch036 [N_Axis]
  Refine = true
  Reversed = true
  Suppressed = false
  Type = 0
FEATURE [PartDesign::Body] Body036  label="StandoffSupport003"
  AllowCompound = false
  Group = -> [Sketch036,Pad036]
  Origin = -> Origin070
  Tip = -> Pad036
FEATURE [Sketcher::SketchObject] Sketch037
  ArcFitTolerance = 1e-06
  AttachmentOffset = pos=(0,0,14) rot=(0,0,1;0rad)
  AttachmentSupport = -> [XY_Plane052]
  FullyConstrained = true
  MakeInternals = false
  MapMode = 5
  Placement = pos=(0,0,14) rot=(0,0,1;0rad)
  sketch-geometry (4):
    g0: LineSegment StartX=19.5 StartY=-14.5 StartZ=0 EndX=19.5 EndY=-17.5 EndZ=0
    g1: LineSegment StartX=19.5 StartY=-17.5 StartZ=0 EndX=20.5 EndY=-17.5 EndZ=0
    g2: LineSegment StartX=20.5 StartY=-17.5 StartZ=0 EndX=20.5 EndY=-14.5 EndZ=0
    g3: LineSegment StartX=20.5 StartY=-14.5 StartZ=0 EndX=19.5 EndY=-14.5 EndZ=0
  constraints (12):
    c: Coincident(g0,g1)
    c: Coincident(g1,g2)
    c: Coincident(g2,g3)
    c: Coincident(g3,g0)
    c: Vertical(g0)
    c: Vertical(g2)
    c: Horizontal(g1)
    c: Horizontal(g3)
    c: DistanceX(g3,g3) = 1
    c: DistanceY(g2,g2) = 3
    c: DistanceX(g-1,g0) = 19.5
    c: DistanceY(g0,g-1) = 14.5
FEATURE [PartDesign::Pad] Pad037  label="Pad038"
  Direction = (0,0,1)
  Length = 3
  Length2 = 10
  Profile = -> Sketch037
  ReferenceAxis = -> Sketch037 [N_Axis]
  Refine = true
  Reversed = true
  Suppressed = false
  Type = 0
FEATURE [PartDesign::Body] Body037  label="StandoffSupport004"
  AllowCompound = false
  Group = -> [Sketch037,Pad037]
  Origin = -> Origin071
  Tip = -> Pad037
FEATURE [Part::MultiFuse] Fusion003  label="Fusion004"
  Refine = true
  Shapes = -> [Cut018,Body034,Body035,Body036,Body037]
FEATURE [Sketcher::SketchObject] Sketch038
  ArcFitTolerance = 1e-06
  AttachmentOffset = pos=(0,0,14.5) rot=(0,0,1;0rad)
  AttachmentSupport = -> [XY_Plane053]
  FullyConstrained = true
  MakeInternals = false
  MapMode = 5
  Placement = pos=(0,0,14.5) rot=(0,0,1;0rad)
  sketch-geometry (6):
    g0: ArcOfCircle CenterX=-15 CenterY=4 CenterZ=0 NormalX=0 NormalY=0 NormalZ=1 AngleXU=0 Radius=4 StartAngle=1e-16 EndAngle=3.14159
    g1: ArcOfCircle CenterX=-15 CenterY=-4 CenterZ=0 NormalX=0 NormalY=0 NormalZ=1 AngleXU=0 Radius=4 StartAngle=3.14159 EndAngle=6.28319
    g2: LineSegment StartX=-11 StartY=4 StartZ=0 EndX=-11 EndY=-4 EndZ=0
    g3: LineSegment StartX=-19 StartY=4 StartZ=0 EndX=-19 EndY=-4 EndZ=0
    g4: Circle CenterX=-15 CenterY=-3.5 CenterZ=0 NormalX=0 NormalY=0 NormalZ=1 AngleXU=0 Radius=1.45
    g5: Circle CenterX=-15 CenterY=3.5 CenterZ=0 NormalX=0 NormalY=0 NormalZ=1 AngleXU=0 Radius=1.45
  constraints (15):
    c: Tangent(g0,g2) = 1.5708
    c: Tangent(g0,g3) = -1.5708
    c: Tangent(g1,g2) = 1.5708
    c: Tangent(g1,g3) = -1.5708
    c: Equal(g0,g1)
    c: Symmetric(g1,g0,g-1)
    c: DistanceY(g2,g2) = 8
    c: Diameter(g1) = 8
    c: DistanceX(g1,g-1) = 15
    c: Diameter(g4) = 2.9
    c: DistanceX(g4,g-1) = 15
    c: DistanceY(g4,g-1) = 3.5
    c: Diameter(g5) = 2.9
    c: DistanceX(g5,g-1) = 15
    c: DistanceY(g-1,g5) = 3.5
FEATURE [PartDesign::Pad] Pad038  label="Pad039"
  Direction = (0,0,1)
  Length = 7
  Length2 = 10
  Profile = -> Sketch038
  ReferenceAxis = -> Sketch038 [N_Axis]
  Refine = true
  Reversed = true
  Suppressed = false
  Type = 0
FEATURE [PartDesign::Body] Body038  label="LoadCellStandoff"
  AllowCompound = false
  Group = -> [Sketch038,Pad038]
  Origin = -> Origin072
  Placement = pos=(0,0,0) rot=(0,0,1;3.14159rad)
  Tip = -> Pad038
FEATURE [Sketcher::SketchObject] Sketch039
  ArcFitTolerance = 1e-06
  AttachmentOffset = pos=(0,0,8) rot=(0,0,1;0rad)
  AttachmentSupport = -> [XY_Plane054]
  FullyConstrained = false
  MakeInternals = false
  MapMode = 5
  Placement = pos=(0,0,8) rot=(0,0,1;0rad)
  sketch-geometry (16):
    g0: LineSegment StartX=-41 StartY=8 StartZ=0 EndX=-41 EndY=-8 EndZ=0
    g1: LineSegment StartX=-41 StartY=-8 StartZ=0 EndX=6.90228 EndY=-8 EndZ=0
    g2: LineSegment StartX=6.90228 StartY=8 StartZ=0 EndX=-41 EndY=8 EndZ=0
    g3: LineSegment StartX=22.4002 StartY=-8 StartZ=0 EndX=40.3566 EndY=-8 EndZ=0
    g4: LineSegment StartX=40.3566 StartY=-8 StartZ=0 EndX=40.3566 EndY=8 EndZ=0
    g5: LineSegment StartX=40.3566 StartY=8 StartZ=0 EndX=22.4905 EndY=8 EndZ=0
    g6: LineSegment StartX=22.4905 StartY=8 StartZ=0 EndX=22.4905 EndY=13.9577 EndZ=0
    g7: LineSegment StartX=22.4905 StartY=13.9577 StartZ=0 EndX=6.90228 EndY=13.9577 EndZ=0
    g8: LineSegment StartX=6.90228 StartY=13.9577 StartZ=0 EndX=6.90228 EndY=8 EndZ=0
    g9: LineSegment StartX=6.90228 StartY=-8 StartZ=0 EndX=6.90228 EndY=-14.043 EndZ=0
    g10: LineSegment StartX=6.90228 StartY=-14.043 StartZ=0 EndX=22.4002 EndY=-14.043 EndZ=0
    g11: LineSegment StartX=22.4002 StartY=-14.043 StartZ=0 EndX=22.4002 EndY=-8 EndZ=0
    g12: LineSegment StartX=9.07991 StartY=11.1814 StartZ=0 EndX=9.07991 EndY=-11.7204 EndZ=0
    g13: LineSegment StartX=9.07991 StartY=-11.7204 StartZ=0 EndX=20.6795 EndY=-11.7204 EndZ=0
    g14: LineSegment StartX=20.6795 StartY=-11.7204 StartZ=0 EndX=20.6795 EndY=11.1814 EndZ=0
    g15: LineSegment StartX=20.6795 StartY=11.1814 StartZ=0 EndX=9.07991 EndY=11.1814 EndZ=0
  constraints (33):
    c: Coincident(g0,g1)
    c: Coincident(g2,g0)
    c: Horizontal(g1)
    c: Horizontal(g2)
    c: DistanceY(g0,g0) = 16
    c: Symmetric(g0,g0,g-1)
    c: Coincident(g3,g4)
    c: Coincident(g4,g5)
    c: Horizontal(g3)
    c: Horizontal(g5)
    c: Equal(g4,g0)
    c: Symmetric(g4,g3,g-1)
    c: Coincident(g6,g7)
    c: Coincident(g7,g8)
    c: Horizontal(g7)
    c: Vertical(g6)
    c: Vertical(g8)
    c: Coincident(g5,g6)
    c: Coincident(g9,g10)
    c: Coincident(g10,g11)
    c: Vertical(g9)
    c: Vertical(g11)
    c: Horizontal(g10)
    c: Coincident(g9,g1)
    c: Coincident(g11,g3)
    c: Coincident(g12,g13)
    c: Coincident(g13,g14)
    c: Coincident(g14,g15)
    c: Coincident(g15,g12)
    c: Vertical(g12)
    c: Vertical(g14)
    c: Horizontal(g13)
    c: Horizontal(g15)
FEATURE [PartDesign::Pad] Pad039  label="Pad040"
  Direction = (0,0,1)
  Length = 2
  Length2 = 10
  Profile = -> Sketch039
  ReferenceAxis = -> Sketch039 [N_Axis]
  Refine = true
  Reversed = true
  Suppressed = false
  Type = 0
FEATURE [PartDesign::Body] Body039  label="LoadCellCutout001"
  AllowCompound = false
  Group = -> [Sketch039,Pad039]
  Origin = -> Origin073
  Tip = -> Pad039
FEATURE [Part::MultiFuse] Fusion004  label="Fusion005"
  Refine = true
  Shapes = -> [Fusion003,Body038]
FEATURE [Part::Cut] Cut019
  Base = -> Fusion004
  Refine = true
  Tool = -> Body039
FEATURE [Sketcher::SketchObject] Sketch040
  ArcFitTolerance = 1e-06
  AttachmentOffset = pos=(0,0,7) rot=(0,0,1;0rad)
  AttachmentSupport = -> [XY_Plane055]
  FullyConstrained = false
  MakeInternals = false
  MapMode = 5
  Placement = pos=(0,0,7) rot=(0,0,1;0rad)
  sketch-geometry (13):
    g0: ArcOfCircle [constr] CenterX=-21.5 CenterY=-8e-16 CenterZ=0 NormalX=0 NormalY=0 NormalZ=1 AngleXU=0 Radius=17 StartAngle=1.5708 EndAngle=4.71239
    g1: ArcOfCircle [constr] CenterX=21.5 CenterY=1.7e-15 CenterZ=0 NormalX=0 NormalY=0 NormalZ=1 AngleXU=0 Radius=17 StartAngle=4.71239 EndAngle=7.85398
    g2: LineSegment [constr] StartX=-21.5 StartY=17 StartZ=0 EndX=21.5 EndY=17 EndZ=0
    g3: LineSegment StartX=-21.5 StartY=17 StartZ=0 EndX=21.5 EndY=17 EndZ=0
    g4: Circle [constr] CenterX=-38.5 CenterY=0 CenterZ=0 NormalX=0 NormalY=0 NormalZ=1 AngleXU=0 Radius=12.5
    g5: Circle [constr] CenterX=38.5 CenterY=0 CenterZ=0 NormalX=0 NormalY=0 NormalZ=1 AngleXU=0 Radius=12.5
    g6: ArcOfCircle CenterX=21.5 CenterY=-2e-16 CenterZ=0 NormalX=0 NormalY=0 NormalZ=1 AngleXU=0 Radius=17 StartAngle=0.488987 EndAngle=1.5708
    g7: ArcOfCircle CenterX=-21.5 CenterY=-1.3e-15 CenterZ=0 NormalX=0 NormalY=0 NormalZ=1 AngleXU=0 Radius=17 StartAngle=1.5708 EndAngle=2.65022
    g8: LineSegment StartX=-21.5 StartY=18 StartZ=0 EndX=21.5 EndY=18 EndZ=0
    g9: LineSegment StartX=-36.4887 StartY=8.02123 StartZ=0 EndX=-37.4887 EndY=8.02123 EndZ=0
    g10: ArcOfCircle CenterX=-22.003 CenterY=1.00744 CenterZ=0 NormalX=0 NormalY=0 NormalZ=1 AngleXU=0 Radius=17 StartAngle=1.54121 EndAngle=2.71631
    g11: LineSegment StartX=36.5078 StartY=7.98544 StartZ=0 EndX=37.5078 EndY=7.98544 EndZ=0
    g12: ArcOfCircle CenterX=22.0059 CenterY=1.00753 CenterZ=0 NormalX=0 NormalY=0 NormalZ=1 AngleXU=0 Radius=17 StartAngle=0.422964 EndAngle=1.60056
  constraints (33):
    c: Tangent(g0,g2) = 1.5708
    c: Tangent(g1,g2) = 1.5708
    c: DistanceX(g2,g2) = 43
    c: Symmetric(g0,g1,g-2)
    c: Symmetric(g0,g0,g-1)
    c: DistanceY(g0,g0) = 34
    c: Coincident(g3,g0)
    c: Coincident(g3,g1)
    c: PointOnObject(g4,g0)
    c: PointOnObject(g4,g-1)
    c: PointOnObject(g5,g-1)
    c: PointOnObject(g5,g1)
    c: Equal(g5,g4)
    c: Diameter(g5) = 25
    c: PointOnObject(g6,g1)
    c: Tangent(g6,g1) = -1.5708
    c: PointOnObject(g7,g0)
    c: Tangent(g7,g0) = -1.5708
    c: Symmetric(g8,g8,g-2)
    c: Equal(g8,g3)
    c: DistanceY(g0,g8) = 1
    c: Coincident(g9,g7)
    c: Horizontal(g9)
    c: DistanceX(g9,g9) = 1
    c: Coincident(g10,g9)
    c: Coincident(g10,g8)
    c: Equal(g10,g7)
    c: Coincident(g11,g6)
    c: Horizontal(g11)
    c: DistanceX(g11,g11) = 1
    c: Coincident(g12,g11)
    c: Coincident(g12,g8)
    c: Equal(g12,g6)
FEATURE [PartDesign::Pad] Pad040  label="Pad041"
  Direction = (0,0,1)
  Length = 1
  Length2 = 10
  Profile = -> Sketch040
  ReferenceAxis = -> Sketch040 [N_Axis]
  Refine = true
  Suppressed = false
  Type = 0
FEATURE [PartDesign::Body] Body040  label="BevelTop1"
  AllowCompound = false
  Group = -> [Sketch040,Pad040]
  Origin = -> Origin074
  Tip = -> Pad040
FEATURE [Sketcher::SketchObject] Sketch041
  ArcFitTolerance = 1e-06
  AttachmentOffset = pos=(0,0,7) rot=(0,0,1;0rad)
  AttachmentSupport = -> [XY_Plane055]
  FullyConstrained = false
  MakeInternals = false
  MapMode = 5
  Placement = pos=(0,0,7) rot=(0,0,1;0rad)
  sketch-geometry (13):
    g0: ArcOfCircle [constr] CenterX=-21.5 CenterY=-8e-16 CenterZ=0 NormalX=0 NormalY=0 NormalZ=1 AngleXU=0 Radius=17 StartAngle=1.5708 EndAngle=4.71239
    g1: ArcOfCircle [constr] CenterX=21.5 CenterY=1.7e-15 CenterZ=0 NormalX=0 NormalY=0 NormalZ=1 AngleXU=0 Radius=17 StartAngle=4.71239 EndAngle=7.85398
    g2: LineSegment [constr] StartX=-21.5 StartY=17 StartZ=0 EndX=21.5 EndY=17 EndZ=0
    g3: LineSegment StartX=-21.5 StartY=17 StartZ=0 EndX=21.5 EndY=17 EndZ=0
    g4: Circle [constr] CenterX=-38.5 CenterY=0 CenterZ=0 NormalX=0 NormalY=0 NormalZ=1 AngleXU=0 Radius=12.5
    g5: Circle [constr] CenterX=38.5 CenterY=0 CenterZ=0 NormalX=0 NormalY=0 NormalZ=1 AngleXU=0 Radius=12.5
    g6: ArcOfCircle CenterX=21.5 CenterY=-2e-16 CenterZ=0 NormalX=0 NormalY=0 NormalZ=1 AngleXU=0 Radius=17 StartAngle=0.488987 EndAngle=1.5708
    g7: ArcOfCircle CenterX=-21.5 CenterY=-1.3e-15 CenterZ=0 NormalX=0 NormalY=0 NormalZ=1 AngleXU=0 Radius=17 StartAngle=1.5708 EndAngle=2.65022
    g8: LineSegment StartX=-21.5 StartY=18 StartZ=0 EndX=21.5 EndY=18 EndZ=0
    g9: LineSegment StartX=-36.4887 StartY=8.02123 StartZ=0 EndX=-37.4887 EndY=8.02123 EndZ=0
    g10: ArcOfCircle CenterX=-22.003 CenterY=1.00744 CenterZ=0 NormalX=0 NormalY=0 NormalZ=1 AngleXU=0 Radius=17 StartAngle=1.54121 EndAngle=2.71631
    g11: LineSegment StartX=36.5078 StartY=7.98544 StartZ=0 EndX=37.5078 EndY=7.98544 EndZ=0
    g12: ArcOfCircle CenterX=22.0059 CenterY=1.00753 CenterZ=0 NormalX=0 NormalY=0 NormalZ=1 AngleXU=0 Radius=17 StartAngle=0.422964 EndAngle=1.60056
  constraints (33):
    c: Tangent(g0,g2) = 1.5708
    c: Tangent(g1,g2) = 1.5708
    c: DistanceX(g2,g2) = 43
    c: Symmetric(g0,g1,g-2)
    c: Symmetric(g0,g0,g-1)
    c: DistanceY(g0,g0) = 34
    c: Coincident(g3,g0)
    c: Coincident(g3,g1)
    c: PointOnObject(g4,g0)
    c: PointOnObject(g4,g-1)
    c: PointOnObject(g5,g-1)
    c: PointOnObject(g5,g1)
    c: Equal(g5,g4)
    c: Diameter(g5) = 25
    c: PointOnObject(g6,g1)
    c: Tangent(g6,g1) = -1.5708
    c: PointOnObject(g7,g0)
    c: Tangent(g7,g0) = -1.5708
    c: Symmetric(g8,g8,g-2)
    c: Equal(g8,g3)
    c: DistanceY(g0,g8) = 1
    c: Coincident(g9,g7)
    c: Horizontal(g9)
    c: DistanceX(g9,g9) = 1
    c: Coincident(g10,g9)
    c: Coincident(g10,g8)
    c: Equal(g10,g7)
    c: Coincident(g11,g6)
    c: Horizontal(g11)
    c: DistanceX(g11,g11) = 1
    c: Coincident(g12,g11)
    c: Coincident(g12,g8)
    c: Equal(g12,g6)
FEATURE [PartDesign::Pad] Pad041  label="Pad042"
  Direction = (0,0,1)
  Length = 1
  Length2 = 10
  Profile = -> Sketch041
  ReferenceAxis = -> Sketch041 [N_Axis]
  Refine = true
  Suppressed = false
  Type = 0
FEATURE [PartDesign::Body] Body041  label="BevelTop002"
  AllowCompound = false
  Group = -> [Sketch041,Pad041]
  Origin = -> Origin075
  Placement = pos=(0,0,0) rot=(0,0,1;3.14159rad)
  Tip = -> Pad041
FEATURE [Part::Cut] Cut020
  Base = -> Cut019
  Refine = true
  Tool = -> Body040
FEATURE [Part::Cut] Cut021  label="Top"
  Base = -> Cut020
  Refine = true
  Tool = -> Body041
FEATURE [Sketcher::SketchObject] Sketch042
  ArcFitTolerance = 1e-06
  AttachmentOffset = pos=(0,0,19) rot=(0,0,1;0rad)
  AttachmentSupport = -> [XZ_Plane056]
  FullyConstrained = true
  MakeInternals = false
  MapMode = 5
  Placement = pos=(0,-19,4.2e-15) rot=(1,0,0;1.5708rad)
  sketch-geometry (4):
    g0: ArcOfCircle CenterX=3.975 CenterY=3.6 CenterZ=0 NormalX=0 NormalY=0 NormalZ=1 AngleXU=0 Radius=1.7 StartAngle=1.5708 EndAngle=4.71239
    g1: ArcOfCircle CenterX=10.375 CenterY=3.6 CenterZ=0 NormalX=0 NormalY=0 NormalZ=1 AngleXU=0 Radius=1.7 StartAngle=4.71239 EndAngle=7.85398
    g2: LineSegment StartX=3.975 StartY=5.3 StartZ=0 EndX=10.375 EndY=5.3 EndZ=0
    g3: LineSegment StartX=3.975 StartY=1.9 StartZ=0 EndX=10.375 EndY=1.9 EndZ=0
  constraints (10):
    c: Tangent(g0,g2) = 1.5708
    c: Tangent(g0,g3) = -1.5708
    c: Tangent(g1,g2) = 1.5708
    c: Tangent(g1,g3) = -1.5708
    c: Equal(g0,g1)
    c: Horizontal(g2)
    c: DistanceY(g0,g0) = 3.4
    c: DistanceX(g2,g2) = 6.4
    c: DistanceX(g-1,g0) = 3.975
    c: DistanceY(g-1,g0) = 5.3
FEATURE [PartDesign::Pad] Pad042  label="Pad043"
  Direction = (0,-1,2e-16)
  Length = 5
  Length2 = 10
  Placement = pos=(0,0,0) rot=(1,0,0;1.5708rad)
  Profile = -> Sketch042
  ReferenceAxis = -> Sketch042 [N_Axis]
  Refine = true
  Reversed = true
  Suppressed = false
  Type = 0
FEATURE [PartDesign::Body] Body042  label="usb_cutout"
  AllowCompound = false
  Group = -> [Sketch042,Pad042]
  Origin = -> Origin076
  Tip = -> Pad042
FEATURE [Part::Cut] Cut022
  Base = -> Cut009
  Refine = true
  Tool = -> Body042
FEATURE [Sketcher::SketchObject] Sketch043
  ArcFitTolerance = 1e-06
  AttachmentOffset = pos=(0,0,-19) rot=(0,0,1;0rad)
  AttachmentSupport = -> [XZ_Plane057]
  FullyConstrained = true
  MakeInternals = false
  MapMode = 5
  Placement = pos=(0,19,-4.2e-15) rot=(1,0,0;1.5708rad)
  sketch-geometry (1):
    g0: Circle CenterX=-2.9 CenterY=1.1 CenterZ=0 NormalX=0 NormalY=0 NormalZ=1 AngleXU=0 Radius=0.6
  constraints (3):
    c: Diameter(g0) = 1.2
    c: DistanceX(g0,g-1) = 2.9
    c: DistanceY(g-1,g0) = 1.1
FEATURE [PartDesign::Pad] Pad043  label="Pad044"
  Direction = (0,-1,2e-16)
  Length = 5
  Length2 = 10
  Placement = pos=(0,0,0) rot=(1,0,0;1.5708rad)
  Profile = -> Sketch043
  ReferenceAxis = -> Sketch043 [N_Axis]
  Refine = true
  Suppressed = false
  Type = 0
FEATURE [PartDesign::Body] Body043  label="led_cutout"
  AllowCompound = false
  Group = -> [Sketch043,Pad043]
  Origin = -> Origin077
  Tip = -> Pad043
FEATURE [Part::Cut] Cut023
  Base = -> Cut022
  Refine = true
  Tool = -> Body043
FEATURE [Sketcher::SketchObject] Sketch044
  ArcFitTolerance = 1e-06
  AttachmentOffset = pos=(0,0,-19) rot=(0,0,1;0rad)
  AttachmentSupport = -> [XZ_Plane058]
  FullyConstrained = true
  MakeInternals = false
  MapMode = 5
  Placement = pos=(0,19,-4.2e-15) rot=(1,0,0;1.5708rad)
  sketch-geometry (4):
    g0: LineSegment StartX=9.5 StartY=4.4 StartZ=0 EndX=4.5 EndY=4.4 EndZ=0
    g1: LineSegment StartX=4.5 StartY=4.4 StartZ=0 EndX=4.5 EndY=1.9 EndZ=0
    g2: LineSegment StartX=4.5 StartY=1.9 StartZ=0 EndX=9.5 EndY=1.9 EndZ=0
    g3: LineSegment StartX=9.5 StartY=1.9 StartZ=0 EndX=9.5 EndY=4.4 EndZ=0
  constraints (12):
    c: Coincident(g0,g1)
    c: Coincident(g1,g2)
    c: Coincident(g2,g3)
    c: Coincident(g3,g0)
    c: Horizontal(g0)
    c: Horizontal(g2)
    c: Vertical(g1)
    c: Vertical(g3)
    c: DistanceX(g0,g0) = 5
    c: DistanceY(g1,g1) = 2.5
    c: DistanceY(g-1,g1) = 1.9
    c: DistanceX(g-1,g0) = 4.5
FEATURE [PartDesign::Pad] Pad044  label="Pad045"
  Direction = (0,-1,2e-16)
  Length = 5
  Length2 = 10
  Placement = pos=(0,0,0) rot=(1,0,0;1.5708rad)
  Profile = -> Sketch044
  ReferenceAxis = -> Sketch044 [N_Axis]
  Refine = true
  Suppressed = false
  Type = 0
FEATURE [PartDesign::Body] Body044  label="switch_cutout"
  AllowCompound = false
  Group = -> [Sketch044,Pad044]
  Origin = -> Origin078
  Tip = -> Pad044
FEATURE [Part::Cut] Cut024
  Base = -> Cut023
  Refine = true
  Tool = -> Body044
FEATURE [Sketcher::SketchObject] Sketch046
  ArcFitTolerance = 1e-06
  AttachmentOffset = pos=(0,0,-5) rot=(0,0,1;0rad)
  AttachmentSupport = -> [XY_Plane060]
  FullyConstrained = true
  MakeInternals = false
  MapMode = 5
  Placement = pos=(0,0,-5) rot=(0,0,1;0rad)
  sketch-geometry (4):
    g0: LineSegment StartX=-17.5 StartY=9.5 StartZ=0 EndX=-17.5 EndY=-9.5 EndZ=0
    g1: LineSegment StartX=-17.5 StartY=-9.5 StartZ=0 EndX=17.5 EndY=-9.5 EndZ=0
    g2: LineSegment StartX=17.5 StartY=-9.5 StartZ=0 EndX=17.5 EndY=9.5 EndZ=0
    g3: LineSegment StartX=17.5 StartY=9.5 StartZ=0 EndX=-17.5 EndY=9.5 EndZ=0
  constraints (11):
    c: Coincident(g0,g1)
    c: Coincident(g1,g2)
    c: Coincident(g2,g3)
    c: Coincident(g3,g0)
    c: Vertical(g0)
    c: Vertical(g2)
    c: Horizontal(g1)
    c: Horizontal(g3)
    c: Symmetric(g1,g0,g-1)
    c: DistanceX(g3,g3) = 35
    c: DistanceY(g0,g0) = 19
FEATURE [PartDesign::Pad] Pad046  label="Pad047"
  Direction = (0,0,1)
  Length = 10
  Length2 = 10
  Profile = -> Sketch046
  ReferenceAxis = -> Sketch046 [N_Axis]
  Refine = true
  Suppressed = false
  Type = 0
FEATURE [PartDesign::Body] Body046  label="window_cutout"
  AllowCompound = false
  Group = -> [Sketch046,Pad046]
  Origin = -> Origin080
  Tip = -> Pad046
FEATURE [Sketcher::SketchObject] Sketch047
  ArcFitTolerance = 1e-06
  AttachmentOffset = pos=(0,0,-5) rot=(0,0,1;0rad)
  AttachmentSupport = -> [XY_Plane061]
  FullyConstrained = true
  MakeInternals = false
  MapMode = 5
  Placement = pos=(0,0,-5) rot=(0,0,1;0rad)
  sketch-geometry (4):
    g0: LineSegment StartX=-17.5 StartY=9.5 StartZ=0 EndX=-17.5 EndY=-9.5 EndZ=0
    g1: LineSegment StartX=-17.5 StartY=-9.5 StartZ=0 EndX=17.5 EndY=-9.5 EndZ=0
    g2: LineSegment StartX=17.5 StartY=-9.5 StartZ=0 EndX=17.5 EndY=9.5 EndZ=0
    g3: LineSegment StartX=17.5 StartY=9.5 StartZ=0 EndX=-17.5 EndY=9.5 EndZ=0
  constraints (11):
    c: Coincident(g0,g1)
    c: Coincident(g1,g2)
    c: Coincident(g2,g3)
    c: Coincident(g3,g0)
    c: Vertical(g0)
    c: Vertical(g2)
    c: Horizontal(g1)
    c: Horizontal(g3)
    c: Symmetric(g1,g0,g-1)
    c: DistanceX(g3,g3) = 35
    c: DistanceY(g0,g0) = 19
FEATURE [PartDesign::Pad] Pad047  label="Pad048"
  Direction = (0,0,1)
  Length = 1.5
  Length2 = 10
  Profile = -> Sketch047
  ReferenceAxis = -> Sketch047 [N_Axis]
  Refine = true
  Suppressed = false
  Type = 0
FEATURE [PartDesign::Body] Body047  label="window"
  AllowCompound = false
  Group = -> [Sketch047,Pad047]
  Origin = -> Origin081
  Tip = -> Pad047
FEATURE [Sketcher::SketchObject] Sketch048
  ArcFitTolerance = 1e-06
  AttachmentOffset = pos=(0,0,-18) rot=(0,0,1;0rad)
  AttachmentSupport = -> [XZ_Plane062]
  FullyConstrained = true
  MakeInternals = false
  MapMode = 5
  Placement = pos=(0,18,-4e-15) rot=(1,0,0;1.5708rad)
  sketch-geometry (1):
    g0: Circle CenterX=-11.2 CenterY=1.6 CenterZ=0 NormalX=0 NormalY=0 NormalZ=1 AngleXU=0 Radius=2.25
  constraints (3):
    c: DistanceX(g0,g-1) = 11.2
    c: DistanceY(g-1,g0) = 1.6
    c: Diameter(g0) = 4.5
FEATURE [PartDesign::Pad] Pad048  label="Pad049"
  Direction = (0,-1,2e-16)
  Length = 3
  Length2 = 10
  Placement = pos=(0,0,0) rot=(1,0,0;1.5708rad)
  Profile = -> Sketch048
  ReferenceAxis = -> Sketch048 [N_Axis]
  Refine = true
  Reversed = true
  Suppressed = false
  Type = 0
FEATURE [PartDesign::Body] Body048  label="button_cutout"
  AllowCompound = false
  Group = -> [Sketch048,Pad048]
  Origin = -> Origin082
  Tip = -> Pad048
FEATURE [Sketcher::SketchObject] Sketch049
  ArcFitTolerance = 1e-06
  AttachmentOffset = pos=(0,0,-17) rot=(0,0,1;0rad)
  AttachmentSupport = -> [XZ_Plane062]
  FullyConstrained = true
  MakeInternals = false
  MapMode = 5
  Placement = pos=(0,17,-3.8e-15) rot=(1,0,0;1.5708rad)
  sketch-geometry (1):
    g0: Circle CenterX=-11.2 CenterY=1.6 CenterZ=0 NormalX=0 NormalY=0 NormalZ=1 AngleXU=0 Radius=3
  constraints (3):
    c: DistanceX(g0,g-1) = 11.2
    c: DistanceY(g-1,g0) = 1.6
    c: Diameter(g0) = 6
FEATURE [PartDesign::Pad] Pad049  label="Pad050"
  Direction = (0,-1,2e-16)
  Length = 1
  Length2 = 10
  Placement = pos=(0,0,0) rot=(1,0,0;1.5708rad)
  Profile = -> Sketch049
  ReferenceAxis = -> Sketch049 [N_Axis]
  Refine = true
  Reversed = true
  Suppressed = false
  Type = 0
FEATURE [PartDesign::Body] Body049  label="button_cutout001"
  AllowCompound = false
  Group = -> [Sketch049,Pad049]
  Origin = -> Origin083
  Tip = -> Pad049
FEATURE [Part::MultiFuse] Fusion005  label="button_cutout_full"
  Refine = true
  Shapes = -> [Body048,Body049]
FEATURE [Sketcher::SketchObject] Sketch050
  ArcFitTolerance = 1e-06
  AttachmentOffset = pos=(0,0,-18) rot=(0,0,1;0rad)
  AttachmentSupport = -> [XZ_Plane062]
  FullyConstrained = true
  MakeInternals = false
  MapMode = 5
  Placement = pos=(0,18,-4e-15) rot=(1,0,0;1.5708rad)
  sketch-geometry (1):
    g0: Circle CenterX=-11.2 CenterY=1.6 CenterZ=0 NormalX=0 NormalY=0 NormalZ=1 AngleXU=0 Radius=2.05
  constraints (3):
    c: DistanceX(g0,g-1) = 11.2
    c: DistanceY(g-1,g0) = 1.6
    c: Diameter(g0) = 4.1
FEATURE [PartDesign::Pad] Pad050  label="Pad051"
  Direction = (0,-1,2e-16)
  Length = 1.4
  Length2 = 10
  Placement = pos=(0,0,0) rot=(1,0,0;1.5708rad)
  Profile = -> Sketch050
  ReferenceAxis = -> Sketch050 [N_Axis]
  Refine = true
  Reversed = true
  Suppressed = false
  Type = 0
FEATURE [PartDesign::Body] Body050  label="button_cutout002"
  AllowCompound = false
  Group = -> [Sketch050,Pad050]
  Origin = -> Origin084
  Tip = -> Pad050
FEATURE [Sketcher::SketchObject] Sketch051
  ArcFitTolerance = 1e-06
  AttachmentOffset = pos=(0,0,-16.8) rot=(0,0,1;0rad)
  AttachmentSupport = -> [XZ_Plane062]
  FullyConstrained = true
  MakeInternals = false
  MapMode = 5
  Placement = pos=(0,16.8,-3.7e-15) rot=(1,0,0;1.5708rad)
  sketch-geometry (1):
    g0: Circle CenterX=-11.2 CenterY=1.6 CenterZ=0 NormalX=0 NormalY=0 NormalZ=1 AngleXU=0 Radius=2.75
  constraints (3):
    c: DistanceX(g0,g-1) = 11.2
    c: DistanceY(g-1,g0) = 1.6
    c: Diameter(g0) = 5.5
FEATURE [PartDesign::Pad] Pad051  label="Pad052"
  Direction = (0,-1,2e-16)
  Length = 1.2
  Length2 = 10
  Placement = pos=(0,0,0) rot=(1,0,0;1.5708rad)
  Profile = -> Sketch051
  ReferenceAxis = -> Sketch051 [N_Axis]
  Refine = true
  Reversed = true
  Suppressed = false
  Type = 0
FEATURE [PartDesign::Body] Body051  label="button_cutout003"
  AllowCompound = false
  Group = -> [Sketch051,Pad051]
  Origin = -> Origin085
  Tip = -> Pad051
FEATURE [Part::MultiFuse] Fusion006  label="button"
  Refine = true
  Shapes = -> [Body050,Body051]
FEATURE [Part::Cut] Cut025
  Base = -> Cut024
  Refine = true
  Tool = -> Fusion005
FEATURE [Sketcher::SketchObject] Sketch052
  ArcFitTolerance = 1e-06
  AttachmentOffset = pos=(0,0,4) rot=(0,0,1;0rad)
  AttachmentSupport = -> [XY_Plane066]
  FullyConstrained = true
  MakeInternals = false
  MapMode = 5
  Placement = pos=(0,0,4) rot=(0,0,1;0rad)
  sketch-geometry (1):
    g0: Circle CenterX=12.85 CenterY=-14 CenterZ=0 NormalX=0 NormalY=0 NormalZ=1 AngleXU=0 Radius=1
  constraints (3):
    c: DistanceX(g-1,g0) = 12.85
    c: DistanceY(g0,g-1) = 14
    c: Diameter(g0) = 2
FEATURE [PartDesign::Pad] Pad052  label="Pad053"
  Direction = (0,0,1)
  Length = 18
  Length2 = 10
  Profile = -> Sketch052
  ReferenceAxis = -> Sketch052 [N_Axis]
  Refine = true
  Suppressed = false
  Type = 0
FEATURE [PartDesign::Body] Body052  label="dfu_access"
  AllowCompound = false
  Group = -> [Sketch052,Pad052]
  Origin = -> Origin086
  Tip = -> Pad052
FEATURE [Part::Cut] Cut026
  Base = -> Cut021
  Refine = true
  Tool = -> Body052
FEATURE [Part::Part2DObjectPython] ShapeString  # Draft 2D object (typed FeaturePython)
  FontFile = <userpath>/Downloads/zephyrean/zephyreg.ttf
  Fuse = false
  Justification = 6
  JustificationReference = 0
  KeepLeftMargin = false
  MakeFace = true
  ObliqueAngle = 0
  Placement = pos=(-11.5,1,16.5) rot=(0,0,1;0rad)
  ScaleToSize = true
  Size = 10
  String = CRUX
  Tracking = 0
FEATURE [Part::Extrusion] Extrude
  Base = -> ShapeString
  Dir = (0,0,1)
  DirMode = 2
  FaceMakerClass = Part::FaceMakerBullseye
  FaceMakerMode = 3
  LengthFwd = 0.5
  LengthRev = 0
  Reversed = true
  Solid = false
  Symmetric = false
FEATURE [Part::Part2DObjectPython] ShapeString001  # Draft 2D object (typed FeaturePython)
  FontFile = <userpath>/Downloads/zephyrean/zephyreg.ttf
  Fuse = false
  Justification = 6
  JustificationReference = 0
  KeepLeftMargin = false
  MakeFace = true
  ObliqueAngle = 0
  Placement = pos=(-14,-11.5,17) rot=(0,0,1;0rad)
  ScaleToSize = true
  Size = 10
  String = TOOLS
  Tracking = 0
FEATURE [Part::Extrusion] Extrude001
  Base = -> ShapeString001
  Dir = (0,0,1)
  DirMode = 2
  FaceMakerClass = Part::FaceMakerBullseye
  FaceMakerMode = 3
  LengthFwd = 0.5
  LengthRev = 0
  Placement = pos=(0,0,-0.5) rot=(0,0,1;0rad)
  Reversed = true
  Solid = false
  Symmetric = false
FEATURE [Part::Feature] path1
  Placement = pos=(0,0,0) rot=(1,0,0;3.14159rad)
  shape: bbox 97.68 x 36.58 x 2e-07 mm, 1 faces, 0 solids (baked)
FEATURE [Part::Feature] path002
  Placement = pos=(0,0,0) rot=(1,0,0;3.14159rad)
  shape: bbox 7.862 x 5.123 x 2e-07 mm, 1 faces, 0 solids (baked)
FEATURE [Part::FeaturePython] Clone  label="path003"  # Draft clone (typed FeaturePython)
  AttacherType = Attacher::AttachEngine3D
  Fuse = false
  Objects = -> [path1]
  Placement = pos=(-22.663,-9.2925,-5) rot=(1,0,0;3.14159rad)
  Scale = (0.45,0.45,0.45)
FEATURE [Part::FeaturePython] Clone001  label="path004"  # Draft clone (typed FeaturePython)
  AttacherType = Attacher::AttachEngine3D
  Fuse = false
  Objects = -> [path002]
  Placement = pos=(-22.6285,-9.3675,-5) rot=(1,0,0;3.14159rad)
  Scale = (0.45,0.45,0.45)
FEATURE [Sketcher::SketchObject] Sketch053
  ArcFitTolerance = 1e-06
  FullyConstrained = false
  MakeInternals = false
  Placement = pos=(0,-6e-16,-5) rot=(0,0,-1;3.14159rad)
  sketch-geometry (86):
    g0: BSplineCurve PolesCount=4 KnotsCount=2 Degree=3 IsPeriodic=0
    g1: BSplineCurve PolesCount=4 KnotsCount=2 Degree=3 IsPeriodic=0
    g2: BSplineCurve PolesCount=4 KnotsCount=2 Degree=3 IsPeriodic=0
    g3: BSplineCurve PolesCount=4 KnotsCount=2 Degree=3 IsPeriodic=0
    g4: BSplineCurve PolesCount=4 KnotsCount=2 Degree=3 IsPeriodic=0
    g5: BSplineCurve PolesCount=4 KnotsCount=2 Degree=3 IsPeriodic=0
    g6: BSplineCurve PolesCount=4 KnotsCount=2 Degree=3 IsPeriodic=0
    g7: BSplineCurve PolesCount=4 KnotsCount=2 Degree=3 IsPeriodic=0
    g8: BSplineCurve PolesCount=4 KnotsCount=2 Degree=3 IsPeriodic=0
    g9: BSplineCurve PolesCount=4 KnotsCount=2 Degree=3 IsPeriodic=0
    g10: BSplineCurve PolesCount=2 KnotsCount=2 Degree=1 IsPeriodic=0
    g11: BSplineCurve PolesCount=2 KnotsCount=2 Degree=1 IsPeriodic=0
    g12: BSplineCurve PolesCount=4 KnotsCount=2 Degree=3 IsPeriodic=0
    g13: BSplineCurve PolesCount=4 KnotsCount=2 Degree=3 IsPeriodic=0
    g14: BSplineCurve PolesCount=4 KnotsCount=2 Degree=3 IsPeriodic=0
    g15: BSplineCurve PolesCount=4 KnotsCount=2 Degree=3 IsPeriodic=0
    g16: BSplineCurve PolesCount=4 KnotsCount=2 Degree=3 IsPeriodic=0
    g17: BSplineCurve PolesCount=4 KnotsCount=2 Degree=3 IsPeriodic=0
    g18: BSplineCurve PolesCount=4 KnotsCount=2 Degree=3 IsPeriodic=0
    g19: BSplineCurve PolesCount=4 KnotsCount=2 Degree=3 IsPeriodic=0
    g20: BSplineCurve PolesCount=4 KnotsCount=2 Degree=3 IsPeriodic=0
    g21: BSplineCurve PolesCount=4 KnotsCount=2 Degree=3 IsPeriodic=0
    g22: BSplineCurve PolesCount=4 KnotsCount=2 Degree=3 IsPeriodic=0
    g23: BSplineCurve PolesCount=4 KnotsCount=2 Degree=3 IsPeriodic=0
    g24: BSplineCurve PolesCount=4 KnotsCount=2 Degree=3 IsPeriodic=0
    g25: BSplineCurve PolesCount=4 KnotsCount=2 Degree=3 IsPeriodic=0
    g26: BSplineCurve PolesCount=4 KnotsCount=2 Degree=3 IsPeriodic=0
    g27: BSplineCurve PolesCount=4 KnotsCount=2 Degree=3 IsPeriodic=0
    g28: BSplineCurve PolesCount=4 KnotsCount=2 Degree=3 IsPeriodic=0
    g29: BSplineCurve PolesCount=4 KnotsCount=2 Degree=3 IsPeriodic=0
    g30: BSplineCurve PolesCount=4 KnotsCount=2 Degree=3 IsPeriodic=0
    g31: BSplineCurve PolesCount=4 KnotsCount=2 Degree=3 IsPeriodic=0
    g32: BSplineCurve PolesCount=4 KnotsCount=2 Degree=3 IsPeriodic=0
    g33: BSplineCurve PolesCount=4 KnotsCount=2 Degree=3 IsPeriodic=0
    g34: BSplineCurve PolesCount=4 KnotsCount=2 Degree=3 IsPeriodic=0
    g35: BSplineCurve PolesCount=2 KnotsCount=2 Degree=1 IsPeriodic=0
    g36: BSplineCurve PolesCount=2 KnotsCount=2 Degree=1 IsPeriodic=0
    g37: BSplineCurve PolesCount=4 KnotsCount=2 Degree=3 IsPeriodic=0
    g38: BSplineCurve PolesCount=4 KnotsCount=2 Degree=3 IsPeriodic=0
    g39: BSplineCurve PolesCount=4 KnotsCount=2 Degree=3 IsPeriodic=0
    g40: BSplineCurve PolesCount=4 KnotsCount=2 Degree=3 IsPeriodic=0
    g41: BSplineCurve PolesCount=2 KnotsCount=2 Degree=1 IsPeriodic=0
    g42: BSplineCurve PolesCount=2 KnotsCount=2 Degree=1 IsPeriodic=0
    g43: BSplineCurve PolesCount=4 KnotsCount=2 Degree=3 IsPeriodic=0
    g44: BSplineCurve PolesCount=4 KnotsCount=2 Degree=3 IsPeriodic=0
    g45: BSplineCurve PolesCount=4 KnotsCount=2 Degree=3 IsPeriodic=0
    g46: BSplineCurve PolesCount=4 KnotsCount=2 Degree=3 IsPeriodic=0
    g47: BSplineCurve PolesCount=4 KnotsCount=2 Degree=3 IsPeriodic=0
    g48: BSplineCurve PolesCount=4 KnotsCount=2 Degree=3 IsPeriodic=0
    g49: BSplineCurve PolesCount=4 KnotsCount=2 Degree=3 IsPeriodic=0
    g50: BSplineCurve PolesCount=4 KnotsCount=2 Degree=3 IsPeriodic=0
    g51: BSplineCurve PolesCount=4 KnotsCount=2 Degree=3 IsPeriodic=0
    g52: BSplineCurve PolesCount=4 KnotsCount=2 Degree=3 IsPeriodic=0
    g53: BSplineCurve PolesCount=4 KnotsCount=2 Degree=3 IsPeriodic=0
    g54: BSplineCurve PolesCount=4 KnotsCount=2 Degree=3 IsPeriodic=0
    g55: BSplineCurve PolesCount=4 KnotsCount=2 Degree=3 IsPeriodic=0
    g56: BSplineCurve PolesCount=4 KnotsCount=2 Degree=3 IsPeriodic=0
    g57: BSplineCurve PolesCount=2 KnotsCount=2 Degree=1 IsPeriodic=0
    g58: BSplineCurve PolesCount=2 KnotsCount=2 Degree=1 IsPeriodic=0
    g59: BSplineCurve PolesCount=4 KnotsCount=2 Degree=3 IsPeriodic=0
    g60: BSplineCurve PolesCount=4 KnotsCount=2 Degree=3 IsPeriodic=0
    g61: BSplineCurve PolesCount=4 KnotsCount=2 Degree=3 IsPeriodic=0
    g62: BSplineCurve PolesCount=4 KnotsCount=2 Degree=3 IsPeriodic=0
    g63: BSplineCurve PolesCount=4 KnotsCount=2 Degree=3 IsPeriodic=0
    g64: BSplineCurve PolesCount=4 KnotsCount=2 Degree=3 IsPeriodic=0
    g65: BSplineCurve PolesCount=2 KnotsCount=2 Degree=1 IsPeriodic=0
    g66: BSplineCurve PolesCount=2 KnotsCount=2 Degree=1 IsPeriodic=0
    g67: BSplineCurve PolesCount=4 KnotsCount=2 Degree=3 IsPeriodic=0
    g68: BSplineCurve PolesCount=4 KnotsCount=2 Degree=3 IsPeriodic=0
    g69: BSplineCurve PolesCount=4 KnotsCount=2 Degree=3 IsPeriodic=0
    g70: BSplineCurve PolesCount=4 KnotsCount=2 Degree=3 IsPeriodic=0
    g71: BSplineCurve PolesCount=4 KnotsCount=2 Degree=3 IsPeriodic=0
    g72: BSplineCurve PolesCount=4 KnotsCount=2 Degree=3 IsPeriodic=0
    g73: BSplineCurve PolesCount=4 KnotsCount=2 Degree=3 IsPeriodic=0
    g74: BSplineCurve PolesCount=4 KnotsCount=2 Degree=3 IsPeriodic=0
    g75: BSplineCurve PolesCount=4 KnotsCount=2 Degree=3 IsPeriodic=0
    g76: BSplineCurve PolesCount=4 KnotsCount=2 Degree=3 IsPeriodic=0
    g77: BSplineCurve PolesCount=4 KnotsCount=2 Degree=3 IsPeriodic=0
    g78: BSplineCurve PolesCount=4 KnotsCount=2 Degree=3 IsPeriodic=0
    g79: BSplineCurve PolesCount=4 KnotsCount=2 Degree=3 IsPeriodic=0
    g80: BSplineCurve PolesCount=4 KnotsCount=2 Degree=3 IsPeriodic=0
    g81: BSplineCurve PolesCount=4 KnotsCount=2 Degree=3 IsPeriodic=0
    g82: BSplineCurve PolesCount=4 KnotsCount=2 Degree=3 IsPeriodic=0
    g83: BSplineCurve PolesCount=4 KnotsCount=2 Degree=3 IsPeriodic=0
    g84: BSplineCurve PolesCount=4 KnotsCount=2 Degree=3 IsPeriodic=0
    g85: BSplineCurve PolesCount=2 KnotsCount=2 Degree=1 IsPeriodic=0
  constraints (86):
    c: Coincident(g0,g1)
    c: Coincident(g1,g2)
    c: Coincident(g2,g3)
    c: Coincident(g3,g4)
    c: Coincident(g4,g5)
    c: Coincident(g5,g6)
    c: Coincident(g6,g7)
    c: Coincident(g7,g8)
    c: Coincident(g8,g9)
    c: Coincident(g9,g10)
    c: Coincident(g10,g11)
    c: Coincident(g11,g12)
    c: Coincident(g12,g13)
    c: Coincident(g13,g14)
    c: Coincident(g14,g15)
    c: Coincident(g15,g16)
    c: Coincident(g16,g17)
    c: Coincident(g17,g18)
    c: Coincident(g18,g19)
    c: Coincident(g19,g20)
    c: Coincident(g20,g21)
    c: Coincident(g21,g22)
    c: Coincident(g22,g23)
    c: Coincident(g23,g24)
    c: Coincident(g24,g25)
    c: Coincident(g25,g26)
    c: Coincident(g26,g27)
    c: Coincident(g27,g28)
    c: Coincident(g28,g29)
    c: Coincident(g29,g30)
    c: Coincident(g30,g31)
    c: Coincident(g31,g32)
    c: Coincident(g32,g33)
    c: Coincident(g33,g34)
    c: Coincident(g34,g35)
    c: Coincident(g35,g36)
    c: Coincident(g36,g37)
    c: Coincident(g37,g38)
    c: Coincident(g38,g39)
    c: Coincident(g39,g40)
    c: Coincident(g40,g41)
    c: Coincident(g41,g42)
    c: Coincident(g42,g43)
    c: Coincident(g43,g44)
    c: Coincident(g44,g45)
    c: Coincident(g45,g46)
    c: Coincident(g46,g47)
    c: Coincident(g47,g48)
    c: Coincident(g48,g49)
    c: Coincident(g49,g50)
    c: Coincident(g50,g51)
    c: Coincident(g51,g52)
    c: Coincident(g52,g53)
    c: Coincident(g53,g54)
    c: Coincident(g54,g55)
    c: Coincident(g55,g56)
    c: Coincident(g56,g57)
    c: Coincident(g57,g58)
    c: Coincident(g58,g59)
    c: Coincident(g59,g60)
    c: Coincident(g60,g61)
    c: Coincident(g61,g62)
    c: Coincident(g62,g63)
    c: Coincident(g63,g64)
    c: Coincident(g64,g65)
    c: Coincident(g65,g66)
    c: Coincident(g66,g67)
    c: Coincident(g67,g68)
    c: Coincident(g68,g69)
    c: Coincident(g69,g70)
    c: Coincident(g70,g71)
    c: Coincident(g71,g72)
    c: Coincident(g72,g73)
    c: Coincident(g73,g74)
    c: Coincident(g74,g75)
    c: Coincident(g75,g76)
    c: Coincident(g76,g77)
    c: Coincident(g77,g78)
    c: Coincident(g78,g79)
    c: Coincident(g79,g80)
    c: Coincident(g80,g81)
    c: Coincident(g81,g82)
    c: Coincident(g82,g83)
    c: Coincident(g83,g84)
    c: Coincident(g84,g85)
    c: Coincident(g85,g0)
FEATURE [Sketcher::SketchObject] Sketch054
  ArcFitTolerance = 1e-06
  FullyConstrained = false
  MakeInternals = false
  Placement = pos=(0,-6e-16,-5) rot=(0,0,-1;3.14159rad)
  sketch-geometry (5):
    g0: BSplineCurve PolesCount=4 KnotsCount=2 Degree=3 IsPeriodic=0
    g1: BSplineCurve PolesCount=4 KnotsCount=2 Degree=3 IsPeriodic=0
    g2: BSplineCurve PolesCount=4 KnotsCount=2 Degree=3 IsPeriodic=0
    g3: BSplineCurve PolesCount=4 KnotsCount=2 Degree=3 IsPeriodic=0
    g4: BSplineCurve PolesCount=4 KnotsCount=2 Degree=3 IsPeriodic=0
  constraints (5):
    c: Coincident(g0,g1)
    c: Coincident(g1,g2)
    c: Coincident(g2,g3)
    c: Coincident(g3,g4)
    c: Coincident(g4,g0)
FEATURE [Part::Extrusion] Extrude002
  Base = -> Sketch053
  Dir = (0,0,1)
  DirMode = 2
  FaceMakerClass = Part::FaceMakerBullseye
  FaceMakerMode = 3
  LengthFwd = 0.5
  LengthRev = 0
  Placement = pos=(0,0,0.5) rot=(0,0,1;0rad)
  Reversed = true
  Solid = true
  Symmetric = false
FEATURE [Part::Extrusion] Extrude003
  Base = -> Sketch054
  Dir = (0,0,1)
  DirMode = 2
  FaceMakerClass = Part::FaceMakerBullseye
  FaceMakerMode = 3
  LengthFwd = 0.5
  LengthRev = 0
  Placement = pos=(0,0,0.5) rot=(0,0,1;0rad)
  Reversed = true
  Solid = true
  Symmetric = false
FEATURE [Part::Part2DObjectPython] ShapeString002  # Draft 2D object (typed FeaturePython)
  FontFile = <userpath>/Downloads/Silverstone-Sans.ttf
  Fuse = false
  Justification = 6
  JustificationReference = 0
  KeepLeftMargin = false
  MakeFace = true
  ObliqueAngle = 0
  Placement = pos=(13.5,19,1.75) rot=(0,0.707107,0.707107;3.14159rad)
  ScaleToSize = true
  Size = 3
  String = O
  Tracking = 0
FEATURE [Part::Part2DObjectPython] ShapeString003  # Draft 2D object (typed FeaturePython)
  FontFile = <userpath>/Downloads/Silverstone-Sans.ttf
  Fuse = false
  Justification = 6
  JustificationReference = 0
  KeepLeftMargin = false
  MakeFace = true
  ObliqueAngle = 0
  Placement = pos=(3,19,1.75) rot=(0,0.707107,0.707107;3.14159rad)
  ScaleToSize = true
  Size = 3
  String = I
  Tracking = 0
FEATURE [Part::Extrusion] Extrude004
  Base = -> ShapeString003
  Dir = (0,1,-2e-16)
  DirMode = 2
  FaceMakerClass = Part::FaceMakerBullseye
  FaceMakerMode = 3
  LengthFwd = 0.5
  LengthRev = 0
  Placement = pos=(0,-0.5,0) rot=(0,0,1;0rad)
  Solid = false
  Symmetric = false
FEATURE [Part::Extrusion] Extrude005
  Base = -> ShapeString002
  Dir = (0,1,-2e-16)
  DirMode = 2
  FaceMakerClass = Part::FaceMakerBullseye
  FaceMakerMode = 3
  LengthFwd = 0.5
  LengthRev = 0
  Placement = pos=(0,-0.5,0) rot=(0,0,1;0rad)
  Solid = false
  Symmetric = false
FEATURE [Part::Cut] Cut032
  Base = -> Cut026
  Refine = true
  Tool = -> Extrude
FEATURE [Part::Cut] Cut033
  Base = -> Cut032
  Refine = true
  Tool = -> Extrude001
FEATURE [Sketcher::SketchObject] Sketch055
  ArcFitTolerance = 1e-06
  AttachmentOffset = pos=(0,0,-4.5) rot=(0,0,1;0rad)
  AttachmentSupport = -> [XY_Plane067]
  FullyConstrained = false
  MakeInternals = false
  MapMode = 5
  Placement = pos=(0,0,-4.5) rot=(0,0,1;0rad)
  sketch-geometry (49):
    g0-g24: Circle [constr] x25 (B-spline internal-alignment scaffolding for g25; pole/knot coordinates omitted)
    g25: BSplineCurve PolesCount=25 KnotsCount=23 Degree=3 IsPeriodic=0
    g26-g48: GeomPoint [constr] x23 (B-spline internal-alignment scaffolding for g25; pole/knot coordinates omitted)
  constraints (9):
    c: Weight(g0) = 1
    c: Equal(g0, g1-g24) x24
    c: InternalAlignment(g0-g24 -> g25) x25
    c: InternalAlignment(g26-g48 -> g25) x23
    c: PointOnObject(g0,g-1)
    c: PointOnObject(g5,g-2)
    c: PointOnObject(g11,g-1)
    c: PointOnObject(g17,g-2)
    c: Coincident(g24,g0)
FEATURE [PartDesign::Pad] Pad053  label="Pad054"
  Direction = (0,0,1)
  Length = 0.5
  Length2 = 10
  Profile = -> Sketch055
  ReferenceAxis = -> Sketch055 [N_Axis]
  Refine = true
  Reversed = true
  Suppressed = false
  Type = 0
FEATURE [PartDesign::Body] Body053  label="LogoOutline"
  AllowCompound = false
  Group = -> [Sketch055,Pad053]
  Origin = -> Origin087
  Tip = -> Pad053
FEATURE [Part::Cut] Cut034
  Base = -> Cut025
  Refine = true
  Tool = -> Body053
FEATURE [Part::MultiFuse] Fusion007
  Refine = true
  Shapes = -> [Cut034,Extrude002]
FEATURE [Part::Cut] Cut035
  Base = -> Fusion007
  Refine = true
  Tool = -> Extrude003
FEATURE [Part::Cut] Cut036
  Base = -> Cut035
  Refine = true
  Tool = -> Extrude005
FEATURE [Part::Cut] Cut037
  Base = -> Cut036
  Refine = true
  Tool = -> Extrude004
FEATURE [Part::Fillet] Fillet
  Base = -> Cut033
  EdgeLinks = -> Cut033 [Edge168,Edge178]
  Edges = 2 edges r=4: [Edge168,Edge178]
FEATURE [Part::Chamfer] Chamfer  label="top"
  Base = -> Fillet
  EdgeLinks = -> Fillet [Edge3,Edge10]
  Edges = 2 edges r=3: [Edge3,Edge10]
FEATURE [Part::Fillet] Fillet001
  Base = -> Cut037
  EdgeLinks = -> Cut037 [Edge277,Edge288]
  Edges = 2 edges r=4: [Edge277,Edge288]
FEATURE [Part::Chamfer] Chamfer001
  Base = -> Fillet001
  EdgeLinks = -> Fillet001 [Edge3,Edge10]
  Edges = 2 edges r=3: [Edge3,Edge10]
FEATURE [Part::Chamfer] Chamfer002  label="bottom"
  Base = -> Chamfer001
  EdgeLinks = -> Chamfer001 [Edge81,Edge100,Edge101,Edge102,Edge103,Edge116]
  Edges = 6 edges r=0.5: [Edge81,Edge100,Edge101,Edge102,Edge103,Edge116]
